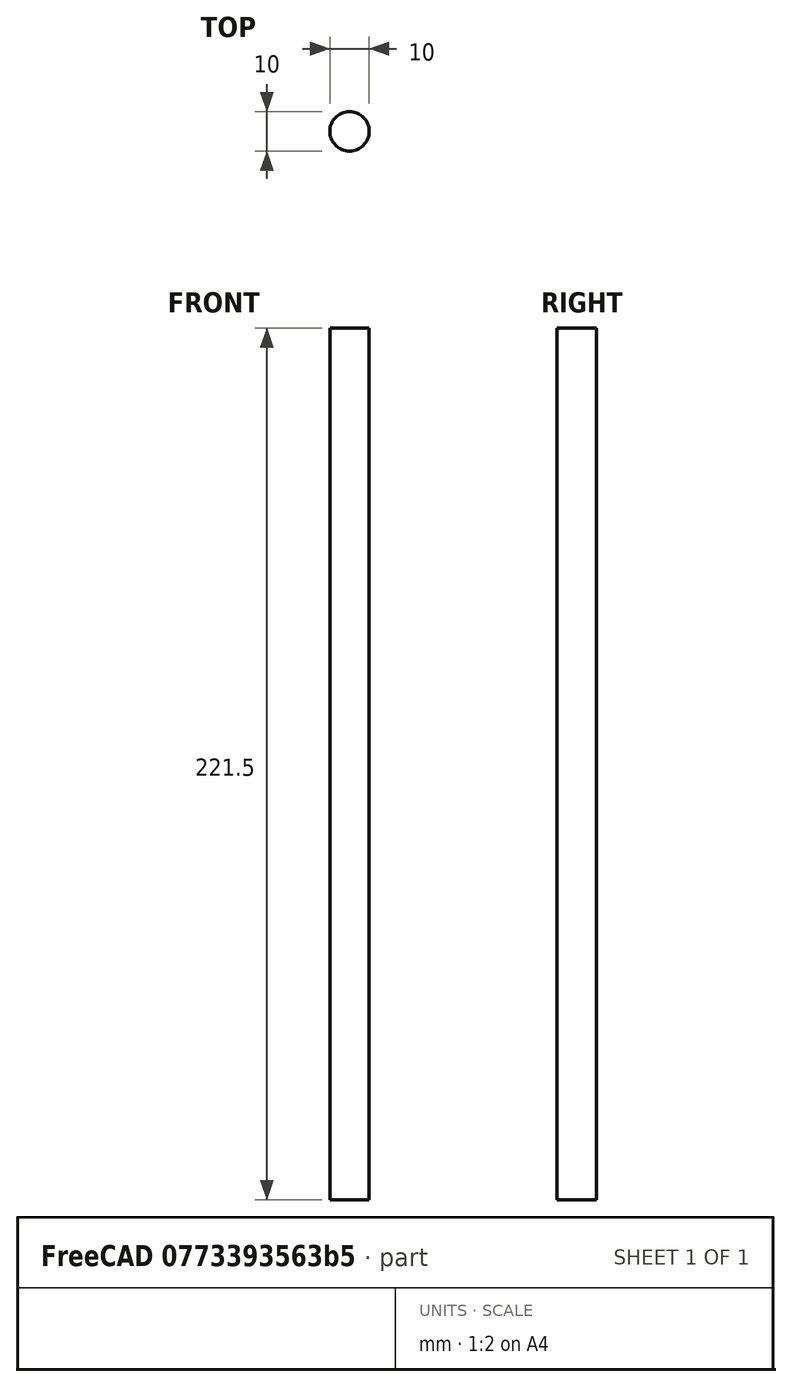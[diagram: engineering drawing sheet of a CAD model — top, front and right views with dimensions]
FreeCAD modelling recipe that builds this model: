
FCSTD DOCUMENT  (FreeCAD 1.0R39109 (Git))
Label: Stator_CoilWinder_Assembly
License: All rights reserved
LicenseURL: http://en.wikipedia.org/wiki/All_rights_reserved
objects: App::Link×12, Part::FeaturePython×8, App::Part×2, Spreadsheet::Sheet×1, Part::Cylinder×1
note: 1 computed .brp shape members not serialized (recipe doc carries the construction recipe); baked Part::Feature solids carry a one-line shape summary decoded from their .brp
EXTERNAL_REF file=Stator_CoilWinder_Cheek.FCStd obj=PolarPattern001Body
EXTERNAL_REF file=Stator_CoilWinder_Spacer.FCStd obj=PadBody001
EXTERNAL_REF file=Stator_CoilWinder_Cheek_Notch.FCStd obj=PolarPattern001Body
EXTERNAL_REF file=../../../Master_of_Puppets.FCStd obj=Alternator
EXTERNAL_REF file=../../../Master_of_Puppets.FCStd obj=Fastener
EXTERNAL_REF file=../../../Master_of_Puppets.FCStd obj=Spreadsheet
EXTERNAL_REF file=../Stator_Coil.FCStd obj=Body001
EXTERNAL_REF file=Stator_CoilWinder_Cheek_Triangular.FCStd obj=PolarPattern001Body
EXTERNAL_REF file=Stator_CoilWinder_Pins_Quadrilateral.FCStd obj=Part
EXTERNAL_REF file=Stator_CoilWinder_Pins_Triangular.FCStd obj=Extrude
EXTERNAL_REF file=Stator_CoilWinder_Spacer_Triangular.FCStd obj=PadBody001
EXTERNAL_REF file=../Stator_Coil_Triangular.FCStd obj=Body
EXTERNAL_REF file=../Stator_Coil_Triangular_Reduced.FCStd obj=Body
EXTERNAL_REF file=../../../Fasteners/Fastener_HexNut_CoilWinder.FCStd obj=Binder
EXTERNAL_REF file=../../../Fasteners/Fastener_Washer_CoilWinder.FCStd obj=Tube

FEATURE [App::Link] Link  label="Stator_CoilWinder_Cheek"
  LinkedObject = -> <external Stator_CoilWinder_Cheek.FCStd>#PolarPattern001Body
  expr: .Placement.Base.z = Spreadsheet.CheekZ
  expr: LinkedObject = Spreadsheet.Stator_CoilWinder_Cheek
FEATURE [App::Link] Link001  label="Stator_CoilWinder_Spacer"
  LinkPlacement = pos=(0,0,12) rot=(0,0,1;0rad)
  LinkedObject = -> <external Stator_CoilWinder_Spacer.FCStd>#PadBody001
  Placement = pos=(0,0,12) rot=(0,0,1;0rad)
  expr: .Placement.Base.z = Spreadsheet.CenterZ
  expr: LinkedObject = Spreadsheet.Stator_CoilWinder_Spacer
FEATURE [App::Link] Link002  label="Stator_CoilWinder_Cheek_Notch"
  LinkPlacement = pos=(0,0,25) rot=(0,0,1;0rad)
  LinkedObject = -> <external Stator_CoilWinder_Cheek_Notch.FCStd>#PolarPattern001Body
  Placement = pos=(0,0,25) rot=(0,0,1;0rad)
  expr: .Placement.Base.z = Spreadsheet.NotchZ
FEATURE [Spreadsheet::Sheet] Spreadsheet
  cells = A1='Inputs; A2='StatorThickness; B2(StatorThickness)==Master_of_Puppets#Spreadsheet.StatorThickness; A3='CoilType; B3(CoilType)==Master_of_Puppets#Spreadsheet.CoilType; A4='CoilWinderCheekThickness; B4(CoilWinderCheekThickness)==Master_of_Puppets#Alternator.CoilWinderCheekThickness; A5='CoilLegWidth; B5(CoilLegWidth)==Master_of_Puppets#Spreadsheet.CoilLegWidth; A6='MagnetWidth; B6(MagnetWidth)==Master_of_Puppets#Spreadsheet.MagnetWidth; A7='MagnetLength; B7(MagnetLength)==Master_of_Puppets#Spreadsheet.MagnetLength; A8='NumberOfCoilsPerPhase; B8(NumberOfCoilsPerPhase)==Master_of_Puppets#Spreadsheet.NumberOfCoilsPerPhase; A9='CoilWinderCenterRodRadius; B9(CoilWinderCenterRodRadius)==Master_of_Puppets#Alternator.CoilWinderCenterRodRadius; A10='CoilWinderHexNutThickness; B10(CoilWinderHexNutThickness)==Master_of_Puppets#Alternator.CoilWinderHexNutThickness; A11='DistanceThreadsExtendFromNuts; B11(DistanceThreadsExtendFromNuts)==Master_of_Puppets#Fastener.DistanceThreadsExtendFromNuts; A12='CoilWinderNumberOfSpacingNuts; B12(CoilWinderNumberOfSpacingNuts)==Master_of_Puppets#Alternator.CoilWinderNumberOfSpacingNuts; A13='CoilWinderSpaceBetweenLayer; B13(CoilWinderSpaceBetweenLayer)==Master_of_Puppets#Alternator.CoilWinderSpaceBetweenLayer; A14='CoilWinderCenterRodLength; B14(CoilWinderCenterRodLength)==Master_of_Puppets#Alternator.CoilWinderCenterRodLength; A15='CoilWinderAssemblyThicknessTotal; B15(CoilWinderAssemblyThicknessTotal)==Master_of_Puppets#Alternator.CoilWinderAssemblyThicknessTotal; A16='CoilWinderNumberOfNutStacks; B16(CoilWinderNumberOfNutStacks)==Master_of_Puppets#Alternator.CoilWinderNumberOfNutStacks; A17='CoilWinderAssemblyThickness; B17(CoilWinderAssemblyThickness)==Master_of_Puppets#Alternator.CoilWinderAssemblyThickness; A18='CoilWinderCoilsAngle; B18(CoilWinderCoilsAngle)==Master_of_Puppets#Alternator.CoilWinderCoilsAngle; A19='DoCoilsOverlap; B19(DoCoilsOverlap)==Master_of_Puppets#Alternator.DoCoilsOverlap; A20='TriangularCoilWinderCircumradius; B20(TriangularCoilWinderCircumradius)==Master_of_Puppets#Alternator.TriangularCoilWinderCircumradius; A21='WasherThickness; B21(WasherThickness)==Master_of_Puppets#Fastener.WasherThickness; A22='Calculated; A23='SpaceBetweenLayers; B23(SpaceBetweenLayers)=0; A24='CheekZ; B24(CheekZ)=0; A25='CenterZ; B25(CenterZ)==CoilWinderCheekThickness + SpaceBetweenLayers; A26='NotchZ; B26(NotchZ)==CenterZ + StatorThickness + SpaceBetweenLayers; A27='Stator_CoilWinder_Cheek; B27(Stator_CoilWinder_Cheek)==CoilType != 3 ? <<Stator_CoilWinder_Cheek>>#<<Stator_CoilWinder_Cheek>>._self : <<Stator_CoilWinder_Cheek_Triangular>>#<<Stator_CoilWinder_Cheek>>._self; A28='Stator_CoilWinder_Spacer; B28(Stator_CoilWinder_Spacer)==CoilType != 3 ? <<Stator_CoilWinder_Spacer>>#<<Stator_CoilWinder_Spacer>>._self : <<Stator_CoilWinder_Spacer_Triangular>>#<<Stator_CoilWinder_Spacer>>._self; A29='Stator_Coil; B29(Stator_Coil)==CoilType != 3 ? <<Stator_Coil>>#<<Stator_Coil>>._self : (DoCoilsOverlap == 1 ? <<Stator_Coil_Triangular_Reduced>>#<<Stator_Coil>>._self : <<Stator_Coil_Triangular>>#<<Stator_Coil>>._self); A30='CoilY; B30(CoilY)==CoilType != 3 ? -(MagnetLength / 2) - CoilLegWidth : -TriangularCoilWinderCircumradius; A31='RodZ; B31(RodZ)==-WasherThickness - CoilWinderHexNutThickness - DistanceThreadsExtendFromNuts; A32='BackWasherNutStackZ; B32(BackWasherNutStackZ)==CoilWinderAssemblyThickness + SpaceBetweenLayers; A33='NutStackZ; B33(NutStackZ)==BackWasherNutStackZ + WasherThickness; A34='FrontWasherNutStackZ; B34(FrontWasherNutStackZ)==NutStackZ + CoilWinderNumberOfSpacingNuts * CoilWinderHexNutThickness; A35='OuterFrontWasherZ; B35(OuterFrontWasherZ)==CoilWinderAssemblyThicknessTotal + SpaceBetweenLayers; A36='NutOuter2Z; B36(NutOuter2Z)==OuterFrontWasherZ + WasherThickness; A37='Pins; B37(Pins)==CoilType != 3 ? <<Stator_CoilWinder_Pins_Quadrilateral>>#<<Stator_CoilWinder_Pins>>._self : <<Stator_CoilWinder_Pins_Triangular>>#<<Stator_CoilWinder_Pins>>._self; A38='PinsZ; B38(PinsZ)==-DistanceThreadsExtendFromNuts; A39='OuterBackNutZ; B39(OuterBackNutZ)==-CoilWinderHexNutThickness - WasherThickness
FEATURE [App::Link] Link003  label="Stator_Coil"
  LinkPlacement = pos=(0,-33.52,12) rot=(0,0,1;0rad)
  LinkedObject = -> <external ../Stator_Coil.FCStd>#Body001
  Placement = pos=(0,-33.52,12) rot=(0,0,1;0rad)
  expr: .Placement.Base.y = Spreadsheet.CoilY
  expr: .Placement.Base.z = Spreadsheet.CenterZ
  expr: LinkedObject = Spreadsheet.Stator_Coil
FEATURE [Part::Cylinder] Cylinder  label="CenterRod"
  Angle = 360
  AttacherType = Attacher::AttachEngine3D
  FirstAngle = 0
  Height = 221.5
  Placement = pos=(0,0,-16.05) rot=(0,0,1;0rad)
  Radius = 5
  SecondAngle = 0
  expr: .Placement.Base.z = Spreadsheet.RodZ
  expr: Height = Spreadsheet.CoilWinderCenterRodLength
  expr: Radius = Spreadsheet.CoilWinderCenterRodRadius
FEATURE [App::Link] Link004  label="Outer_Nut_Back"
  LinkPlacement = pos=(0,0,-11.05) rot=(0,0,1;0rad)
  LinkedObject = -> <external ../../../Fasteners/Fastener_HexNut_CoilWinder.FCStd>#Binder
  Placement = pos=(0,0,-11.05) rot=(0,0,1;0rad)
  expr: .Placement.Base.z = Spreadsheet.OuterBackNutZ
FEATURE [App::Link] Link005  label="Fastener_HexNut_Spacing"
  LinkedObject = -> Link004
FEATURE [Part::FeaturePython] Array  label="NutStack"  # Draft array (typed FeaturePython)
  AlwaysSyncPlacement = false
  Angle = 360
  ArrayType = 0
  Axis = (0,0,1)
  Base = -> Link005
  Center = (0,0,0)
  Count = 4
  ExpandArray = false
  Fuse = false
  IntervalAxis = (0,0,0)
  IntervalX = (100,0,0)
  IntervalY = (0,100,0)
  IntervalZ = (0,0,8.55)
  NumberCircles = 3
  NumberPolar = 5
  NumberX = 1
  NumberY = 1
  NumberZ = 4
  Placement = pos=(0,0,39.5) rot=(0,0,1;0rad)
  PlacementList = 4 placements: arithmetic series from (0,0,0) step (0,0,8.55) to (0,0,25.65)
  RadialDistance = 50
  ScaleList = (4) [(1,1,1),(1,1,1),(1,1,1),(1,1,1)]
  Symmetry = 1
  TangentialDistance = 25
  expr: .IntervalZ.z = Spreadsheet.CoilWinderHexNutThickness
  expr: .Placement.Base.z = Spreadsheet.NutStackZ
  expr: NumberZ = Spreadsheet.CoilWinderNumberOfSpacingNuts
FEATURE [App::Link] Link006  label="Outer_Nut_Front"
  LinkPlacement = pos=(0,0,191.9) rot=(0,0,1;0rad)
  LinkedObject = -> Link004
  Placement = pos=(0,0,191.9) rot=(0,0,1;0rad)
  expr: .Placement.Base.z = Spreadsheet.NutOuter2Z
FEATURE [Part::FeaturePython] Array003  label="Stator_CoilWinder_Cheeks"  # Draft array (typed FeaturePython)
  AlwaysSyncPlacement = false
  Angle = 360
  ArrayType = 0
  Axis = (0,0,1)
  Base = -> Link
  Center = (0,0,0)
  Count = 3
  ExpandArray = false
  Fuse = false
  IntervalAxis = (0,0,0)
  IntervalX = (100,0,0)
  IntervalY = (0,100,0)
  IntervalZ = (0,0,76.2)
  NumberCircles = 3
  NumberPolar = 5
  NumberX = 1
  NumberY = 1
  NumberZ = 3
  PlacementList = 3 placements: arithmetic series from (0,0,0) step (0,0,76.2) to (0,0,152.4)
  RadialDistance = 50
  ScaleList = (3) [(1,1,1),(1,1,1),(1,1,1)]
  Symmetry = 1
  TangentialDistance = 25
  expr: .IntervalZ.z = Spreadsheet.CoilWinderSpaceBetweenLayer
  expr: NumberZ = Spreadsheet.NumberOfCoilsPerPhase
FEATURE [Part::FeaturePython] Array004  label="Stator_CoilWinder_Cheek_Spacers"  # Draft array (typed FeaturePython)
  AlwaysSyncPlacement = false
  Angle = 360
  ArrayType = 0
  Axis = (0,0,1)
  Base = -> Link001
  Center = (0,0,0)
  Count = 3
  ExpandArray = false
  Fuse = false
  IntervalAxis = (0,0,0)
  IntervalX = (100,0,0)
  IntervalY = (0,100,0)
  IntervalZ = (0,0,76.2)
  NumberCircles = 3
  NumberPolar = 5
  NumberX = 1
  NumberY = 1
  NumberZ = 3
  PlacementList = 3 placements: arithmetic series from (0,0,12) step (0,0,76.2) to (0,0,164.4)
  RadialDistance = 50
  ScaleList = (3) [(1,1,1),(1,1,1),(1,1,1)]
  Symmetry = 1
  TangentialDistance = 25
  expr: .IntervalZ.z = Spreadsheet.CoilWinderSpaceBetweenLayer
  expr: NumberZ = Spreadsheet.NumberOfCoilsPerPhase
FEATURE [Part::FeaturePython] Array005  label="Stator_CoilWinder_Cheek_Notches"  # Draft array (typed FeaturePython)
  AlwaysSyncPlacement = false
  Angle = 360
  ArrayType = 0
  Axis = (0,0,1)
  Base = -> Link002
  Center = (0,0,0)
  Count = 3
  ExpandArray = false
  Fuse = false
  IntervalAxis = (0,0,0)
  IntervalX = (100,0,0)
  IntervalY = (0,100,0)
  IntervalZ = (0,0,76.2)
  NumberCircles = 3
  NumberPolar = 5
  NumberX = 1
  NumberY = 1
  NumberZ = 3
  PlacementList = 3 placements: arithmetic series from (0,0,25) step (0,0,76.2) to (0,0,177.4)
  RadialDistance = 50
  ScaleList = (3) [(1,1,1),(1,1,1),(1,1,1)]
  Symmetry = 1
  TangentialDistance = 25
  expr: .IntervalZ.z = Spreadsheet.CoilWinderSpaceBetweenLayer
  expr: NumberZ = Spreadsheet.NumberOfCoilsPerPhase
FEATURE [Part::FeaturePython] Array006  label="Stator_Coils"  # Draft array (typed FeaturePython)
  AlwaysSyncPlacement = false
  Angle = 360
  ArrayType = 0
  Axis = (0,0,1)
  Base = -> Link003
  Center = (0,0,0)
  Count = 3
  ExpandArray = false
  Fuse = false
  IntervalAxis = (0,0,0)
  IntervalX = (100,0,0)
  IntervalY = (0,100,0)
  IntervalZ = (0,0,76.2)
  NumberCircles = 3
  NumberPolar = 5
  NumberX = 1
  NumberY = 1
  NumberZ = 3
  Placement = pos=(0,0,0) rot=(0,0,1;1.5708rad)
  PlacementList = 3 placements: arithmetic series from (0,-33.52,12) step (0,0,76.2) to (0,-33.52,164.4)
  RadialDistance = 50
  ScaleList = (3) [(1,1,1),(1,1,1),(1,1,1)]
  Symmetry = 1
  TangentialDistance = 25
  expr: .IntervalZ.z = Spreadsheet.CoilWinderSpaceBetweenLayer
  expr: .Placement.Rotation.Angle = Spreadsheet.CoilWinderCoilsAngle
  expr: NumberZ = Spreadsheet.NumberOfCoilsPerPhase
FEATURE [App::Link] Link007  label="Pins"
  LinkPlacement = pos=(0,0,-5) rot=(0,0,1;0rad)
  LinkedObject = -> <external Stator_CoilWinder_Pins_Quadrilateral.FCStd>#Part
  Placement = pos=(0,0,-5) rot=(0,0,1;0rad)
  expr: .Placement.Base.z = Spreadsheet.PinsZ
  expr: LinkedObject = Spreadsheet.Pins
FEATURE [App::Part] Part003  label="Rods"
  Group = -> [Cylinder,Link007]
  Origin = -> Origin003
FEATURE [App::Link] Link008  label="Outer_Washer_Back"
  LinkPlacement = pos=(0,0,-2.5) rot=(0,0,1;0rad)
  LinkedObject = -> <external ../../../Fasteners/Fastener_Washer_CoilWinder.FCStd>#Tube
  Placement = pos=(0,0,-2.5) rot=(0,0,1;0rad)
  expr: .Placement.Base.z = -Spreadsheet.WasherThickness
FEATURE [App::Link] Link009  label="Outer_Washer_Front"
  LinkPlacement = pos=(0,0,189.4) rot=(0,0,1;0rad)
  LinkedObject = -> Link008
  Placement = pos=(0,0,189.4) rot=(0,0,1;0rad)
  expr: .Placement.Base.z = Spreadsheet.OuterFrontWasherZ
FEATURE [App::Link] Link010  label="Washer_Back_Inner"
  LinkPlacement = pos=(0,0,37) rot=(0,0,1;0rad)
  LinkedObject = -> Link008
  Placement = pos=(0,0,37) rot=(0,0,1;0rad)
  expr: .Placement.Base.z = Spreadsheet.BackWasherNutStackZ
FEATURE [App::Link] Link011  label="Washer_Front_Inner"
  LinkPlacement = pos=(0,0,73.7) rot=(0,0,1;0rad)
  LinkedObject = -> Link010
  Placement = pos=(0,0,73.7) rot=(0,0,1;0rad)
  expr: .Placement.Base.z = Spreadsheet.FrontWasherNutStackZ
FEATURE [Part::FeaturePython] Array007  label="NutStacks"  # Draft array (typed FeaturePython)
  AlwaysSyncPlacement = false
  Angle = 360
  ArrayType = 0
  Axis = (0,0,1)
  Base = -> Array
  Center = (0,0,0)
  Count = 2
  ExpandArray = false
  Fuse = false
  IntervalAxis = (0,0,0)
  IntervalX = (0,0,0)
  IntervalY = (0,100,0)
  IntervalZ = (0,0,76.2)
  NumberCircles = 3
  NumberPolar = 5
  NumberX = 1
  NumberY = 1
  NumberZ = 2
  PlacementList = 2 placements: [(0,0,39.5),(0,0,115.7)]
  RadialDistance = 50
  ScaleList = (2) [(1,1,1),(1,1,1)]
  Symmetry = 1
  TangentialDistance = 25
  expr: .IntervalZ.z = Spreadsheet.CoilWinderSpaceBetweenLayer
  expr: NumberZ = Spreadsheet.CoilWinderNumberOfNutStacks
FEATURE [Part::FeaturePython] Array008  label="InnerBackWashers"  # Draft array (typed FeaturePython)
  AlwaysSyncPlacement = false
  Angle = 360
  ArrayType = 0
  Axis = (0,0,1)
  Base = -> Link010
  Center = (0,0,0)
  Count = 2
  ExpandArray = false
  Fuse = false
  IntervalAxis = (0,0,0)
  IntervalX = (100,0,0)
  IntervalY = (0,100,0)
  IntervalZ = (0,0,76.2)
  NumberCircles = 3
  NumberPolar = 5
  NumberX = 1
  NumberY = 1
  NumberZ = 2
  PlacementList = 2 placements: [(0,0,37),(0,0,113.2)]
  RadialDistance = 50
  ScaleList = (2) [(1,1,1),(1,1,1)]
  Symmetry = 1
  TangentialDistance = 25
  expr: .IntervalZ.z = Spreadsheet.CoilWinderSpaceBetweenLayer
  expr: NumberZ = Spreadsheet.CoilWinderNumberOfNutStacks
FEATURE [Part::FeaturePython] Array009  label="InnerFrontWashers"  # Draft array (typed FeaturePython)
  AlwaysSyncPlacement = false
  Angle = 360
  ArrayType = 0
  Axis = (0,0,1)
  Base = -> Link011
  Center = (0,0,0)
  Count = 2
  ExpandArray = false
  Fuse = false
  IntervalAxis = (0,0,0)
  IntervalX = (100,0,0)
  IntervalY = (0,100,0)
  IntervalZ = (0,0,76.2)
  NumberCircles = 3
  NumberPolar = 5
  NumberX = 1
  NumberY = 1
  NumberZ = 2
  PlacementList = 2 placements: [(0,0,73.7),(0,0,149.9)]
  RadialDistance = 50
  ScaleList = (2) [(1,1,1),(1,1,1)]
  Symmetry = 1
  TangentialDistance = 25
  expr: .IntervalZ.z = Spreadsheet.CoilWinderSpaceBetweenLayer
  expr: NumberZ = Spreadsheet.CoilWinderNumberOfNutStacks
FEATURE [App::Part] Part  label="Stator_CoilWinder_Assembly"
  Group = -> [Link,Array003,Link001,Array004,Link003,Array006,Link002,Array005,Link004,Part003,Link008,Link009,Link006,Link010,Array008,Link005,Array,Array007,Link011,Array009]
  Origin = -> Origin

RESOLVED EXTERNAL PARTS (link-assembly join: the EXTERNAL_REF files above that resolve inside this repo's crawl, each included once):
---- part ../../../Fasteners/Fastener_HexNut_CoilWinder.FCStd = doc fcstd_accbea4014fd ----
FCSTD DOCUMENT  (FreeCAD 0.20R29177 (Git))
Label: Fastener_HexNut_CoilWinder
License: All rights reserved
LicenseURL: http://en.wikipedia.org/wiki/All_rights_reserved
objects: PartDesign::SubShapeBinder×1
note: 1 computed .brp shape members not serialized (recipe doc carries the construction recipe); baked Part::Feature solids carry a one-line shape summary decoded from their .brp
EXTERNAL_REF file=Fastener_HexNut.FCStd obj=Body

FEATURE [PartDesign::SubShapeBinder] Binder  label="Fastener_HexNut"
  BindCopyOnChange = 2
  BindMode = 0
  ClaimChildren = false
  Fuse = false
  MakeFace = true
  OffsetFill = false
  OffsetIntersection = false
  OffsetJoinType = 0
  OffsetOpenResult = false
  PartialLoad = false
  Relative = true
  Support = -> [<external Fastener_HexNut.FCStd>#Body]
  Variant = 3
  _Version = 2
---- part ../../../Master_of_Puppets.FCStd = doc fcstd_6404554055c4 (61625 chars; too large to inline — full recipe in that document) ----
---- part ../Stator_Coil.FCStd = doc fcstd_4f31de19f594 ----
FCSTD DOCUMENT  (FreeCAD 0.21R33771 (Git))
Label: Stator_Coil
License: All rights reserved
LicenseURL: http://en.wikipedia.org/wiki/All_rights_reserved
objects: Sketcher::SketchObject×1, PartDesign::Pad×1, Spreadsheet::Sheet×1, PartDesign::Mirrored×1, PartDesign::Body×1, Part::Refine×1
note: 6 computed .brp shape members not serialized (recipe doc carries the construction recipe); baked Part::Feature solids carry a one-line shape summary decoded from their .brp
EXTERNAL_REF file=../../Master_of_Puppets.FCStd obj=Alternator
EXTERNAL_REF file=../../Master_of_Puppets.FCStd obj=Spreadsheet

FEATURE [Sketcher::SketchObject] Sketch
  FullyConstrained = true
  MapMode = 5
  Support = -> [XY_Plane]
  expr: Constraints[13] = Spreadsheet.CoilLegWidth
  expr: Constraints[27] = Spreadsheet.CoilHoleWidthAtOuterRadius / 2 - Spreadsheet.CoilWinderPinRadius
  expr: Constraints[30] = Spreadsheet.CoilHoleWidthAtInnerRadius / 2 - Spreadsheet.CoilWinderPinRadius
  expr: Constraints[31] = Spreadsheet.CoilLegWidth
  expr: Constraints[32] = Spreadsheet.CoilLegWidth
  expr: Constraints[4] = Spreadsheet.CoilWinderPinRadius
  expr: Constraints[5] = Spreadsheet.HoleLength
  sketch-geometry (12):
    g0: LineSegment StartX=0 StartY=89.13 StartZ=0 EndX=14.815 EndY=89.13 EndZ=0
    g1: LineSegment StartX=17.2898 StartY=86.2756 StartZ=0 EndX=9.69975 EndY=33.2756 EndZ=0
    g2: LineSegment StartX=7.225 StartY=31.13 StartZ=0 EndX=0 EndY=31.13 EndZ=0
    g3: ArcOfCircle CenterX=14.815 CenterY=86.63 CenterZ=0 NormalX=0 NormalY=0 NormalZ=1 AngleXU=0 Radius=2.5 StartAngle=6.14094 EndAngle=7.85398
    g4: ArcOfCircle CenterX=7.225 CenterY=33.63 CenterZ=0 NormalX=0 NormalY=0 NormalZ=1 AngleXU=0 Radius=2.5 StartAngle=4.71239 EndAngle=6.14094
    g5: LineSegment StartX=0 StartY=120.26 StartZ=0 EndX=17.6214 EndY=120.26 EndZ=0
    g6: LineSegment StartX=48.437 StartY=84.717 StartZ=0 EndX=40.131 EndY=26.717 EndZ=0
    g7: LineSegment StartX=9.31539 StartY=0 StartZ=0 EndX=0 EndY=0 EndZ=0
    g8: ArcOfCircle CenterX=17.6214 CenterY=89.13 CenterZ=0 NormalX=0 NormalY=0 NormalZ=1 AngleXU=0 Radius=31.13 StartAngle=6.14094 EndAngle=7.85398
    g9: ArcOfCircle CenterX=9.31539 CenterY=31.13 CenterZ=0 NormalX=0 NormalY=0 NormalZ=1 AngleXU=0 Radius=31.13 StartAngle=4.71239 EndAngle=6.14094
    g10: LineSegment StartX=0 StartY=120.26 StartZ=0 EndX=0 EndY=89.13 EndZ=0
    g11: LineSegment StartX=0 StartY=31.13 StartZ=0 EndX=0 EndY=0 EndZ=0
  constraints (33):
    c: Horizontal(g0)
    c: Horizontal(g2)
    c: Tangent(g1,g3) = 1.5708
    c: Tangent(g1,g4) = 1.5708
    c: Radius(g3) = 2.5
    c: DistanceY(g2,g0) = 58
    c: Horizontal(g5)
    c: Horizontal(g7)
    c: Parallel(g1,g6)
    c: Tangent(g5,g8) = 1.5708
    c: Tangent(g6,g8) = 1.5708
    c: Tangent(g6,g9) = 1.5708
    c: Tangent(g7,g9) = 1.5708
    c: Radius(g8) = 31.13
    c: Coincident(g7,g-1)
    c: PointOnObject(g2,g-2)
    c: PointOnObject(g0,g-2)
    c: PointOnObject(g5,g-2)
    c: Coincident(g10,g5)
    c: Coincident(g10,g0)
    c: Coincident(g11,g2)
    c: Coincident(g11,g7)
    c: Equal(g4,g3)
    c: Equal(g8,g9)
    c: Equal(g11,g10)
    c: Vertical(g0,g3)
    c: Coincident(g3,g0)
    c: DistanceX(g0,g0) = 14.815
    c: Coincident(g2,g4)
    c: Vertical(g4,g2)
    c: DistanceX(g2,g2) = 7.225
    c: DistanceY(g7,g2) = 31.13
    c: Distance(g6,g1) = 31.13
FEATURE [PartDesign::Pad] Pad
  AllowMultiFace = false
  Direction = (0,0,1)
  Length = 14.8
  Length2 = 100
  Profile = -> Sketch
  Type = 0
  expr: Length = Spreadsheet.CoilThickness
FEATURE [Spreadsheet::Sheet] Spreadsheet
  cells = A1='Inputs; A2='CoilLegWidth; B2(CoilLegWidth)==Master_of_Puppets#Spreadsheet.CoilLegWidth; A3='MagnetLength; B3(MagnetLength)==Master_of_Puppets#Spreadsheet.MagnetLength; A4='CoilHoleWidthAtOuterRadius; B4(CoilHoleWidthAtOuterRadius)==Master_of_Puppets#Spreadsheet.CoilHoleWidthAtOuterRadius; A5='CoilHoleWidthAtInnerRadius; B5(CoilHoleWidthAtInnerRadius)==Master_of_Puppets#Spreadsheet.CoilHoleWidthAtInnerRadius; A6='CoilWinderPinRadius; B6(CoilWinderPinRadius)==Master_of_Puppets#Alternator.CoilWinderPinRadius; A7='CoilThickness; B7(CoilThickness)==Master_of_Puppets#Alternator.CoilThickness; A8='Calculated; A9='HoleLength; B9(HoleLength)==MagnetLength; A10='MiddleLength; B10(MiddleLength)==CoilLegWidth + HoleLength / 2
FEATURE [PartDesign::Mirrored] Mirrored
  BaseFeature = -> Pad
  MirrorPlane = -> Sketch [V_Axis]
  Originals = -> [Pad]
FEATURE [PartDesign::Body] Body
  Group = -> [Sketch,Pad,Mirrored]
  Origin = -> Origin
  Tip = -> Mirrored
FEATURE [Part::Refine] Body001  label="Stator_Coil"
  Source = -> Body
---- part ../Stator_Coil_Triangular.FCStd = doc fcstd_6ed8b2cba0b0 ----
FCSTD DOCUMENT  (FreeCAD 0.21R33771 (Git))
Label: Stator_Coil_Triangular
License: All rights reserved
LicenseURL: http://en.wikipedia.org/wiki/All_rights_reserved
objects: Sketcher::SketchObject×1, PartDesign::Pad×1, PartDesign::Body×1, Spreadsheet::Sheet×1
note: 4 computed .brp shape members not serialized (recipe doc carries the construction recipe); baked Part::Feature solids carry a one-line shape summary decoded from their .brp
EXTERNAL_REF file=../../Master_of_Puppets.FCStd obj=Alternator
EXTERNAL_REF file=../../Master_of_Puppets.FCStd obj=Spreadsheet

FEATURE [Sketcher::SketchObject] Sketch
  FullyConstrained = true
  MapMode = 5
  Support = -> [XY_Plane]
  expr: Constraints[0] = Spreadsheet.CoilWinderPinRadius
  expr: Constraints[15] = Spreadsheet.CoilLegWidth
  expr: Constraints[25] = Spreadsheet.MagnetWidth
  expr: Constraints[29] = Spreadsheet.MagnetLength
  expr: Constraints[2] = Spreadsheet.InnerBottomArcRadius
  sketch-geometry (18):
    g0: Circle CenterX=-22.5 CenterY=72.5 CenterZ=0 NormalX=0 NormalY=0 NormalZ=1 AngleXU=0 Radius=2.5
    g1: Circle CenterX=22.5 CenterY=72.5 CenterZ=0 NormalX=0 NormalY=0 NormalZ=1 AngleXU=0 Radius=2.5
    g2: Circle CenterX=0 CenterY=4 CenterZ=0 NormalX=0 NormalY=0 NormalZ=1 AngleXU=0 Radius=4
    g3: LineSegment StartX=3.82539 StartY=2.83108 StartZ=0 EndX=24.8909 EndY=71.7694 EndZ=0
    g4: LineSegment StartX=-22.5 StartY=75 StartZ=0 EndX=22.5 EndY=75 EndZ=0
    g5: LineSegment StartX=-3.82539 StartY=2.83108 StartZ=0 EndX=-24.8909 EndY=71.7694 EndZ=0
    g6: ArcOfCircle CenterX=0 CenterY=4 CenterZ=0 NormalX=0 NormalY=0 NormalZ=1 AngleXU=0 Radius=4 StartAngle=3.43815 EndAngle=5.98663
    g7: LineSegment StartX=-22.5 StartY=100.92 StartZ=0 EndX=22.5 EndY=100.92 EndZ=0
    g8: LineSegment StartX=-49.6794 StartY=64.1948 StartZ=0 EndX=-28.6139 EndY=-4.74355 EndZ=0
    g9: LineSegment StartX=49.6794 StartY=64.1948 StartZ=0 EndX=28.6139 EndY=-4.74355 EndZ=0
    g10: ArcOfCircle CenterX=-22.5 CenterY=72.5 CenterZ=0 NormalX=0 NormalY=0 NormalZ=1 AngleXU=0 Radius=28.42 StartAngle=1.5708 EndAngle=3.43815
    g11: ArcOfCircle CenterX=22.5 CenterY=72.5 CenterZ=0 NormalX=0 NormalY=0 NormalZ=1 AngleXU=0 Radius=28.42 StartAngle=5.98663 EndAngle=7.85398
    g12: ArcOfCircle CenterX=0 CenterY=4 CenterZ=0 NormalX=0 NormalY=0 NormalZ=1 AngleXU=0 Radius=29.92 StartAngle=3.43815 EndAngle=5.98663
    g13: ArcOfCircle CenterX=-22.5 CenterY=72.5 CenterZ=0 NormalX=0 NormalY=0 NormalZ=1 AngleXU=0 Radius=2.5 StartAngle=1.5708 EndAngle=3.14159
    g14: ArcOfCircle CenterX=-22.5 CenterY=72.5 CenterZ=0 NormalX=0 NormalY=0 NormalZ=1 AngleXU=0 Radius=2.5 StartAngle=3.14159 EndAngle=3.43815
    g15: ArcOfCircle CenterX=22.5 CenterY=72.5 CenterZ=0 NormalX=0 NormalY=0 NormalZ=1 AngleXU=0 Radius=2.5 StartAngle=5.98663 EndAngle=6.28319
    g16: ArcOfCircle CenterX=22.5 CenterY=72.5 CenterZ=0 NormalX=0 NormalY=0 NormalZ=1 AngleXU=0 Radius=2.5 StartAngle=9e-16 EndAngle=1.5708
    g17: GeomPoint X=-22.5 Y=75 Z=0
  constraints (39):
    c: Radius(g0) = 2.5
    c: Equal(g1,g0)
    c: Radius(g2) = 4
    c: Tangent(g3,g1) = -1.5708
    c: Tangent(g5,g0) = 1.5708
    c: Coincident(g6,g2)
    c: Horizontal(g4)
    c: Equal(g6,g2)
    c: Tangent(g6,g5) = 1.5708
    c: Tangent(g3,g6) = -1.5708
    c: Tangent(g4,g0) = 1.5708
    c: Horizontal(g7)
    c: Parallel(g9,g3)
    c: Tangent(g12,g9) = 1.5708
    c: Tangent(g12,g8) = -1.5708
    c: DistanceY(g4,g7) = 25.92
    c: Tangent(g10,g7) = 1.5708
    c: Tangent(g10,g8) = -1.5708
    c: Tangent(g11,g9) = 1.5708
    c: Tangent(g11,g7) = 1.5708
    c: Coincident(g13,g10)
    c: Coincident(g13,g4)
    c: Coincident(g14,g5)
    c: Coincident(g15,g11)
    c: Coincident(g15,g3)
    c: DistanceX(g13,g15) = 50
    c: Horizontal(g15,g13)
    c: Tangent(g14,g13) = -1.5708
    c: Coincident(g14,g0)
    c: Distance(g-1,g4) = 75
    c: Coincident(g6,g12)
    c: PointOnObject(g6,g-2)
    c: Tangent(g16,g15) = -1.5708
    c: Coincident(g1,g11)
    c: Tangent(g16,g4) = 1.5708
    c: Horizontal(g15,g11)
    c: Coincident(g17,g4)
    c: Symmetric(g10,g11,g-2)
    c: PointOnObject(g-1,g6)
FEATURE [PartDesign::Pad] Pad
  AllowMultiFace = false
  Direction = (0,0,1)
  Length = 13.8
  Length2 = 100
  Profile = -> Sketch
  Type = 0
  expr: Length = Spreadsheet.CoilThickness
FEATURE [PartDesign::Body] Body  label="Stator_Coil"
  Group = -> [Sketch,Pad]
  Origin = -> Origin
  Tip = -> Pad
FEATURE [Spreadsheet::Sheet] Spreadsheet
  cells = A1='Inputs; A2='CoilLegWidth; B2(CoilLegWidth)==Master_of_Puppets#Spreadsheet.CoilLegWidth; A3='CoilHoleWidthAtOuterRadius; B3(CoilHoleWidthAtOuterRadius)==Master_of_Puppets#Spreadsheet.CoilHoleWidthAtOuterRadius; A4='CoilHoleWidthAtInnerRadius; B4(CoilHoleWidthAtInnerRadius)==Master_of_Puppets#Spreadsheet.CoilHoleWidthAtInnerRadius; A5='MagnetWidth; B5(MagnetWidth)==Master_of_Puppets#Spreadsheet.MagnetWidth; A6='CoilWinderPinRadius; B6(CoilWinderPinRadius)==Master_of_Puppets#Alternator.CoilWinderPinRadius; A7='CoilThickness; B7(CoilThickness)==Master_of_Puppets#Alternator.CoilThickness; A8='MagnetLength; B8(MagnetLength)==Master_of_Puppets#Alternator.MagnetLength; A9='CoilType; B9(CoilType)==Master_of_Puppets#Alternator.CoilType; A10='Calculated; A11='InnerBottomArcRadius; B11(InnerBottomArcRadius)==CoilType == 3 ? CoilHoleWidthAtInnerRadius / 2 : 4; C11='Duplicated in Stator_Coil_Triangular_Reduced
---- part ../Stator_Coil_Triangular_Reduced.FCStd = doc fcstd_347f9b8b952c ----
FCSTD DOCUMENT  (FreeCAD 1.0R39109 (Git))
Label: Stator_Coil_Triangular_Reduced
License: All rights reserved
LicenseURL: http://en.wikipedia.org/wiki/All_rights_reserved
objects: Sketcher::SketchObject×1, PartDesign::Pad×1, PartDesign::Body×1, Spreadsheet::Sheet×1
note: 6 computed .brp shape members not serialized (recipe doc carries the construction recipe); baked Part::Feature solids carry a one-line shape summary decoded from their .brp
EXTERNAL_REF file=../../Master_of_Puppets.FCStd obj=Alternator
EXTERNAL_REF file=../../Master_of_Puppets.FCStd obj=Spreadsheet

FEATURE [Sketcher::SketchObject] Sketch
  ArcFitTolerance = 0
  AttachmentSupport = -> [XY_Plane]
  FullyConstrained = true
  MakeInternals = false
  MapMode = 5
  expr: Constraints[25] = Spreadsheet.CoilLegWidth
  expr: Constraints[27] = Spreadsheet.CoilLegWidth
  expr: Constraints[2] = Spreadsheet.CoilWinderPinRadius
  expr: Constraints[33] = Spreadsheet.CornerCircleRadius
  expr: Constraints[34] = Spreadsheet.CornerCircleRadius
  expr: Constraints[35] = Spreadsheet.CornerCircleRadius
  expr: Constraints[60] = Spreadsheet.CoilLegWidth
  expr: Constraints[61] = Spreadsheet.VerticalDimension
  expr: Constraints[63] = Spreadsheet.HorizontalDistanceBetweenPins
  expr: Constraints[6] = Spreadsheet.InnerBottomArcRadius
  sketch-geometry (24):
    g0: Circle [constr] CenterX=0 CenterY=18.125 CenterZ=0 NormalX=0 NormalY=0 NormalZ=1 AngleXU=0 Radius=18.125
    g1: Circle [constr] CenterX=-12.5 CenterY=27.5 CenterZ=0 NormalX=0 NormalY=0 NormalZ=1 AngleXU=0 Radius=2.5
    g2: Circle [constr] CenterX=12.5 CenterY=27.5 CenterZ=0 NormalX=0 NormalY=0 NormalZ=1 AngleXU=0 Radius=2.5
    g3: Circle [constr] CenterX=0 CenterY=4 CenterZ=0 NormalX=0 NormalY=0 NormalZ=1 AngleXU=0 Radius=4
    g4: LineSegment StartX=3.63174 StartY=2.32355 StartZ=0 EndX=14.7698 EndY=26.4522 EndZ=0
    g5: LineSegment StartX=-12.5 StartY=30 StartZ=0 EndX=12.5 EndY=30 EndZ=0
    g6: LineSegment StartX=-3.63174 StartY=2.32355 StartZ=0 EndX=-14.7698 EndY=26.4522 EndZ=0
    g7: ArcOfCircle CenterX=-12.5 CenterY=27.5 CenterZ=0 NormalX=0 NormalY=0 NormalZ=1 AngleXU=0 Radius=2.5 StartAngle=1.5708 EndAngle=3.57406
    g8: ArcOfCircle CenterX=12.5 CenterY=27.5 CenterZ=0 NormalX=0 NormalY=0 NormalZ=1 AngleXU=0 Radius=2.5 StartAngle=5.85072 EndAngle=7.85398
    g9: ArcOfCircle CenterX=0 CenterY=4 CenterZ=0 NormalX=0 NormalY=0 NormalZ=1 AngleXU=0 Radius=4 StartAngle=3.57406 EndAngle=5.85072
    g10: LineSegment [constr] StartX=10.9259 StartY=18.125 StartZ=0 EndX=20.0052 EndY=13.9339 EndZ=0
    g11: LineSegment [constr] StartX=-10.9259 StartY=18.125 StartZ=0 EndX=-20.0052 EndY=13.9339 EndZ=0
    g12: Circle [constr] CenterX=-14.5 CenterY=29 CenterZ=0 NormalX=0 NormalY=0 NormalZ=1 AngleXU=0 Radius=10
    g13: Circle [constr] CenterX=14.5 CenterY=29 CenterZ=0 NormalX=0 NormalY=0 NormalZ=1 AngleXU=0 Radius=10
    g14: ArcOfCircle CenterX=34.3876 CenterY=39.0423 CenterZ=0 NormalX=0 NormalY=0 NormalZ=1 AngleXU=0 Radius=59.9083 StartAngle=3.34419 EndAngle=3.57406
    g15: ArcOfCircle CenterX=-14.5 CenterY=29 CenterZ=0 NormalX=0 NormalY=0 NormalZ=1 AngleXU=0 Radius=10 StartAngle=1.70851 EndAngle=3.34419
    g16: ArcOfCircle CenterX=76.5816 CenterY=58.5195 CenterZ=0 NormalX=0 NormalY=0 NormalZ=1 AngleXU=0 Radius=106.381 StartAngle=3.57406 EndAngle=3.79409
    g17: Circle [constr] CenterX=0 CenterY=0 CenterZ=0 NormalX=0 NormalY=0 NormalZ=1 AngleXU=0 Radius=10
    g18: ArcOfCircle CenterX=0 CenterY=0 CenterZ=0 NormalX=0 NormalY=0 NormalZ=1 AngleXU=0 Radius=10 StartAngle=3.79409 EndAngle=5.63069
    g19: ArcOfCircle CenterX=-34.3877 CenterY=39.0423 CenterZ=0 NormalX=0 NormalY=0 NormalZ=1 AngleXU=0 Radius=59.9085 StartAngle=5.85072 EndAngle=6.08059
    g20: ArcOfCircle CenterX=14.5 CenterY=29 CenterZ=0 NormalX=0 NormalY=0 NormalZ=1 AngleXU=0 Radius=10 StartAngle=6.08059 EndAngle=7.71627
    g21: ArcOfCircle CenterX=-76.5816 CenterY=58.5195 CenterZ=0 NormalX=0 NormalY=0 NormalZ=1 AngleXU=0 Radius=106.381 StartAngle=5.63069 EndAngle=5.85072
    g22: ArcOfCircle CenterX=0 CenterY=-75.6253 CenterZ=0 NormalX=0 NormalY=0 NormalZ=1 AngleXU=0 Radius=115.625 StartAngle=1.5708 EndAngle=1.70851
    g23: ArcOfCircle CenterX=0 CenterY=-75.6249 CenterZ=0 NormalX=0 NormalY=0 NormalZ=1 AngleXU=0 Radius=115.625 StartAngle=1.43308 EndAngle=1.5708
  constraints (64):
    c: PointOnObject(g13,g0)
    c: PointOnObject(g12,g0)
    c: Radius(g1) = 2.5
    c: PointOnObject(g12,g1)
    c: Equal(g2,g1)
    c: Tangent(g2,g0)
    c: Radius(g3) = 4
    c: Tangent(g4,g2) = -1.5708
    c: Tangent(g6,g1) = 1.5708
    c: Coincident(g7,g6)
    c: Coincident(g8,g2)
    c: Coincident(g8,g4)
    c: Coincident(g9,g3)
    c: Coincident(g5,g7)
    c: Coincident(g8,g5)
    c: Horizontal(g5)
    c: Vertical(g7,g5)
    c: Vertical(g8,g5)
    c: Vertical(g0,g9)
    c: Equal(g9,g3)
    c: Tangent(g9,g6) = 1.5708
    c: Tangent(g4,g9) = -1.5708
    c: Tangent(g5,g1) = 1.5708
    c: Tangent(g0,g7)
    c: PointOnObject(g10,g4)
    c: Distance(g10) = 10
    c: PointOnObject(g11,g6)
    c: Distance(g11) = 10
    c: Horizontal(g11,g0)
    c: Horizontal(g10,g0)
    c: Perpendicular(g6,g11)
    c: Perpendicular(g4,g10)
    c: PointOnObject(g22,g-2)
    c: Radius(g12) = 10
    c: Radius(g13) = 10
    c: Radius(g17) = 10
    c: Tangent(g16,g17) = -1.5708
    c: Coincident(g18,g16)
    c: Tangent(g21,g18) = -1.5708
    c: Tangent(g15,g14) = -1.5708
    c: Tangent(g19,g20) = -1.5708
    c: Tangent(g22,g15) = -1.5708
    c: PointOnObject(g14,g12)
    c: Tangent(g23,g20) = -1.5708
    c: PointOnObject(g19,g13)
    c: Coincident(g16,g11)
    c: Perpendicular(g16,g11)
    c: Tangent(g14,g16) = -1.5708
    c: Tangent(g19,g21) = -1.5708
    c: Coincident(g19,g10)
    c: Perpendicular(g21,g10)
    c: Tangent(g23,g22) = -1.5708
    c: Coincident(g-1,g18)
    c: Coincident(g17,g18)
    c: PointOnObject(g9,g-2)
    c: Coincident(g20,g13)
    c: Coincident(g15,g12)
    c: PointOnObject(g20,g8)
    c: PointOnObject(g18,g9)
    c: PointOnObject(g18,g0)
    c: Distance(g22,g5) = 10
    c: Distance(g18,g5) = 30
    c: Perpendicular(g22,g-2)
    c: DistanceX(g7,g8) = 25
FEATURE [PartDesign::Pad] Pad
  AllowMultiFace = false
  Direction = (0,0,1)
  Length = 12.8
  Length2 = 100
  Profile = -> Sketch
  Suppressed = false
  Type = 0
  expr: Length = Spreadsheet.CoilThickness
FEATURE [PartDesign::Body] Body  label="Stator_Coil"
  AllowCompound = false
  Group = -> [Sketch,Pad]
  Origin = -> Origin
  Tip = -> Pad
FEATURE [Spreadsheet::Sheet] Spreadsheet
  cells = A1='Inputs; A2='CoilHoleWidthAtOuterRadius; B2(CoilHoleWidthAtOuterRadius)==Master_of_Puppets#Spreadsheet.CoilHoleWidthAtOuterRadius; A3='CoilHoleWidthAtInnerRadius; B3(CoilHoleWidthAtInnerRadius)==Master_of_Puppets#Spreadsheet.CoilHoleWidthAtInnerRadius; A4='MagnetWidth; B4(MagnetWidth)==Master_of_Puppets#Spreadsheet.MagnetWidth; A5='MagnetLength; B5(MagnetLength)==Master_of_Puppets#Spreadsheet.MagnetLength; A6='CoilType; B6(CoilType)==Master_of_Puppets#Spreadsheet.CoilType; A7='SmallestMagnetDimension; B7(SmallestMagnetDimension)==Master_of_Puppets#Alternator.SmallestMagnetDimension; A8='CoilLegWidth; B8(CoilLegWidth)==CoilType != 3 ? SmallestMagnetDimension / 2 : Master_of_Puppets#Spreadsheet.CoilLegWidth; C8='Prevent this from breaking when not triangular coils; A9='CoilWinderPinRadius; B9(CoilWinderPinRadius)==Master_of_Puppets#Alternator.CoilWinderPinRadius; A10='CoilThickness; B10(CoilThickness)==Master_of_Puppets#Alternator.CoilThickness; A11='CoilLegWidthReduced; B11(CoilLegWidthReduced)==Master_of_Puppets#Alternator.CoilLegWidthReduced; A12='HorizontalDistanceBetweenPins; B12(HorizontalDistanceBetweenPins)==Master_of_Puppets#Alternator.TriangularHorizontalDistanceBetweenPins; A13='LargestMagnetDimension; B13(LargestMagnetDimension)==Master_of_Puppets#Alternator.LargestMagnetDimension; A14='Calculated; A15='CornerCircleRadius; B15(CornerCircleRadius)==CoilType != 3 ? CoilLegWidth : CoilLegWidthReduced; C15='Prevent this from breaking when not triangular coils; A16='InnerBottomArcRadius; B16(InnerBottomArcRadius)==CoilType == 3 ? CoilHoleWidthAtInnerRadius / 2 : 4; C16='Duplicated in Stator_Coil_Triangular_Reduced; A17='VerticalDimension; B17(VerticalDimension)==CoilType != 3 ? LargestMagnetDimension : MagnetLength; C17='Prevent this from breaking when not triangular coils
---- part Stator_CoilWinder_Cheek.FCStd = doc fcstd_5f320d548366 ----
FCSTD DOCUMENT  (FreeCAD 1.0R39109 (Git))
Label: Stator_CoilWinder_Cheek
Comment: Back Cheek
License: All rights reserved
LicenseURL: http://en.wikipedia.org/wiki/All_rights_reserved
objects: Sketcher::SketchObject×4, PartDesign::Pocket×3, TechDraw::DrawViewDimension×3, PartDesign::Mirrored×2, PartDesign::Pad×1, Spreadsheet::Sheet×1, PartDesign::Body×1, TechDraw::DrawSVGTemplate×1, TechDraw::DrawProjGroupItem×1, TechDraw::DrawPage×1
note: 31 computed .brp shape members not serialized (recipe doc carries the construction recipe); baked Part::Feature solids carry a one-line shape summary decoded from their .brp
EXTERNAL_REF file=../../../Master_of_Puppets.FCStd obj=Alternator
EXTERNAL_REF file=../../../Master_of_Puppets.FCStd obj=Spreadsheet

FEATURE [Sketcher::SketchObject] Sketch
  ArcFitTolerance = 0
  AttachmentSupport = -> [XY_Plane001]
  FullyConstrained = true
  MakeInternals = false
  MapMode = 5
  expr: Constraints[1] = Spreadsheet.CoilWinderDiskRadius
  sketch-geometry (1):
    g0: Circle CenterX=0 CenterY=0 CenterZ=0 NormalX=0 NormalY=0 NormalZ=1 AngleXU=0 Radius=60.9591
  constraints (2):
    c: Coincident(g0,g-1)
    c: Radius(g0) = 60.9591
FEATURE [PartDesign::Pad] Pad
  AllowMultiFace = false
  Direction = (0,0,1)
  Length = 12
  Length2 = 100
  Profile = -> Sketch
  Suppressed = false
  Type = 0
  expr: Length = Spreadsheet.CoilWinderCheekThickness
FEATURE [Sketcher::SketchObject] Sketch001  label="CenterHoleSketch"
  ArcFitTolerance = 0
  AttachmentSupport = -> [XY_Plane001]
  FullyConstrained = true
  MakeInternals = false
  MapMode = 5
  Placement = pos=(0,0,0) rot=(0,1,0;3.14159rad)
  expr: Constraints[1] = Spreadsheet.CoilWinderCenterRodRadius
  sketch-geometry (1):
    g0: Circle CenterX=0 CenterY=0 CenterZ=0 NormalX=0 NormalY=0 NormalZ=1 AngleXU=0 Radius=5
  constraints (2):
    c: Coincident(g0,g-1)
    c: Radius(g0) = 5
FEATURE [PartDesign::Pocket] Pocket  label="CenterHolePocket"
  AllowMultiFace = false
  BaseFeature = -> Pad
  Direction = (0,0,1)
  Length = 5
  Length2 = 100
  Profile = -> Sketch001
  Suppressed = false
  Type = 1
FEATURE [Sketcher::SketchObject] Sketch002  label="PinHolesSketch"
  ArcFitTolerance = 0
  AttachmentSupport = -> [XY_Plane001]
  FullyConstrained = true
  MakeInternals = false
  MapMode = 5
  Placement = pos=(0,0,0) rot=(0,1,0;3.14159rad)
  expr: Constraints[0] = Spreadsheet.CoilWinderPinRadius
  expr: Constraints[1] = Spreadsheet.RectangularVerticalDistanceOfHolesFromCenter
  expr: Constraints[2] = Spreadsheet.OuterHorizontalDistanceFromCenter
  expr: Constraints[4] = Spreadsheet.RectangularVerticalDistanceOfHolesFromCenter
  expr: Constraints[5] = Spreadsheet.InnerHorizontalDistanceFromCenter
  sketch-geometry (2):
    g0: Circle CenterX=12.5 CenterY=20.5 CenterZ=0 NormalX=0 NormalY=0 NormalZ=1 AngleXU=0 Radius=2.5
    g1: Circle CenterX=12.5 CenterY=-20.5 CenterZ=0 NormalX=0 NormalY=0 NormalZ=1 AngleXU=0 Radius=2.5
  constraints (6):
    c: Radius(g0) = 2.5
    c: DistanceY(g-1,g0) = 20.5
    c: DistanceX(g-1,g0) = 12.5
    c: Equal(g0,g1)
    c: DistanceY(g1,g-1) = 20.5
    c: DistanceX(g-1,g1) = 12.5
FEATURE [Spreadsheet::Sheet] Spreadsheet
  cells = A1='Inputs; A2='Spreadsheet; A3='MagnetWidth; B3(MagnetWidth)==Master_of_Puppets#Spreadsheet.MagnetWidth; A4='MagnetLength; B4(MagnetLength)==Master_of_Puppets#Spreadsheet.MagnetLength; A5='CoilHoleWidthAtOuterRadius; B5(CoilHoleWidthAtOuterRadius)==Master_of_Puppets#Spreadsheet.CoilHoleWidthAtOuterRadius; A6='CoilHoleWidthAtInnerRadius; B6(CoilHoleWidthAtInnerRadius)==Master_of_Puppets#Spreadsheet.CoilHoleWidthAtInnerRadius; A7='CoilType; B7(CoilType)==Master_of_Puppets#Spreadsheet.CoilType; A8='Alternator; A9='CoilWinderDiskRadius; B9(CoilWinderDiskRadius)==Master_of_Puppets#Alternator.CoilWinderDiskRadius; A10='CoilWinderCenterRodRadius; B10(CoilWinderCenterRodRadius)==Master_of_Puppets#Alternator.CoilWinderCenterRodRadius; A11='CoilWinderPinRadius; B11(CoilWinderPinRadius)==Master_of_Puppets#Alternator.CoilWinderPinRadius; A12='CoilWinderDiskTapeNotchWidth; B12(CoilWinderDiskTapeNotchWidth)==Master_of_Puppets#Alternator.CoilWinderDiskTapeNotchWidth; A13='CoilWinderDiskFillet; B13(CoilWinderDiskFillet)==Master_of_Puppets#Alternator.CoilWinderDiskFillet; A14='RectangularVerticalDistanceOfHolesFromCenter; B14(RectangularVerticalDistanceOfHolesFromCenter)==Master_of_Puppets#Alternator.RectangularVerticalDistanceOfHolesFromCenter; A15='CoilWinderCheekThickness; B15(CoilWinderCheekThickness)==Master_of_Puppets#Alternator.CoilWinderCheekThickness; A16='OuterHorizontalDistanceBetweenCenterOfSmallHoles; B16(OuterHorizontalDistanceBetweenCenterOfSmallHoles)==Master_of_Puppets#Alternator.OuterHorizontalDistanceBetweenCenterOfSmallHoles; A17='InnerHorizontalDistanceBetweenCenterOfSmallHoles; B17(InnerHorizontalDistanceBetweenCenterOfSmallHoles)==Master_of_Puppets#Alternator.InnerHorizontalDistanceBetweenCenterOfSmallHoles; A18='Calculated; A19='CoilWinderDiskSmallHoleDiameter; B19(CoilWinderDiskSmallHoleDiameter)==CoilWinderPinRadius * 2; A20='OuterHorizontalDistanceFromCenter; B20(OuterHorizontalDistanceFromCenter)==OuterHorizontalDistanceBetweenCenterOfSmallHoles / 2; A21='InnerHorizontalDistanceFromCenter; B21(InnerHorizontalDistanceFromCenter)==InnerHorizontalDistanceBetweenCenterOfSmallHoles / 2; A22='SmallestOuterDimension; B22(SmallestOuterDimension)==min(CoilHoleWidthAtOuterRadius; MagnetLength); A23='TapeNotchOuterDistanceFromCenter; B23(TapeNotchOuterDistanceFromCenter)==(SmallestOuterDimension - CoilWinderDiskSmallHoleDiameter) / 2; A24='SmallestInnerDimension; B24(SmallestInnerDimension)==min(CoilHoleWidthAtInnerRadius; MagnetLength); A25='TapeNotchInnerDistanceFromCenter; B25(TapeNotchInnerDistanceFromCenter)==CoilType != 3 ? (SmallestInnerDimension - CoilWinderDiskSmallHoleDiameter) / 2 : TapeNotchOuterDistanceFromCenter
FEATURE [Sketcher::SketchObject] Sketch005  label="TapeNotchSketch"
  ArcFitTolerance = 0
  AttachmentSupport = -> [XY_Plane001]
  FullyConstrained = true
  MakeInternals = false
  MapMode = 5
  Placement = pos=(0,0,0) rot=(0,1,0;3.14159rad)
  expr: Constraints[13] = Spreadsheet.CoilWinderDiskFillet
  expr: Constraints[17] = Spreadsheet.CoilWinderDiskFillet
  expr: Constraints[23] = Spreadsheet.OuterHorizontalDistanceFromCenter
  expr: Constraints[24] = Spreadsheet.InnerHorizontalDistanceFromCenter
  expr: Constraints[25] = Spreadsheet.RectangularVerticalDistanceOfHolesFromCenter * 2
  expr: Constraints[26] = Spreadsheet.RectangularVerticalDistanceOfHolesFromCenter
  expr: Constraints[7] = Spreadsheet.CoilWinderDiskTapeNotchWidth
  expr: Constraints[9] = Spreadsheet.CoilWinderDiskRadius
  sketch-geometry (10):
    g0: LineSegment StartX=12.5 StartY=10.5 StartZ=0 EndX=49.6227 EndY=10.5 EndZ=0
    g1: LineSegment StartX=12.5 StartY=-10.5 StartZ=0 EndX=49.6227 EndY=-10.5 EndZ=0
    g2: GeomPoint [constr] X=12.5 Y=0 Z=0
    g3: LineSegment StartX=12.5 StartY=10.5 StartZ=0 EndX=12.5 EndY=0 EndZ=0
    g4: LineSegment StartX=12.5 StartY=0 StartZ=0 EndX=12.5 EndY=-10.5 EndZ=0
    g5: Circle [constr] CenterX=0 CenterY=0 CenterZ=0 NormalX=0 NormalY=0 NormalZ=1 AngleXU=0 Radius=60.9591
    g6: ArcOfCircle CenterX=0 CenterY=0 CenterZ=0 NormalX=0 NormalY=0 NormalZ=1 AngleXU=0 Radius=60.9591 StartAngle=5.92633 EndAngle=6.64004
    g7: ArcOfCircle CenterX=49.6227 CenterY=18.5 CenterZ=0 NormalX=0 NormalY=0 NormalZ=1 AngleXU=0 Radius=8 StartAngle=4.71239 EndAngle=6.64003
    g8: ArcOfCircle CenterX=49.6227 CenterY=-18.5 CenterZ=0 NormalX=0 NormalY=0 NormalZ=1 AngleXU=0 Radius=8 StartAngle=5.92633 EndAngle=7.85398
    g9: LineSegment [constr] StartX=12.5 StartY=-20.5 StartZ=0 EndX=12.5 EndY=20.5 EndZ=0
  constraints (27):
    c: Parallel(g1,g0)
    c: Coincident(g3,g0)
    c: Coincident(g3,g2)
    c: Coincident(g4,g3)
    c: Coincident(g4,g1)
    c: Equal(g3,g4)
    c: Perpendicular(g3,g0)
    c: Distance(g1,g0) = 21
    c: Coincident(g5,g-1)
    c: Radius(g5) = 60.9591
    c: PointOnObject(g6,g5)
    c: Coincident(g6,g5)
    c: Tangent(g0,g7) = -1.5708
    c: Radius(g7) = 8
    c: Coincident(g6,g7)
    c: Tangent(g7,g5)
    c: Tangent(g1,g8) = 1.5708
    c: Radius(g8) = 8
    c: Tangent(g6,g8) = -1.5708
    c: PointOnObject(g1,g9)
    c: PointOnObject(g0,g9)
    c: PointOnObject(g2,g9)
    c: PointOnObject(g2,g-1)
    c: DistanceX(g9) = 12.5
    c: DistanceX(g-1,g9) = 12.5
    c: DistanceY(g9,g9) = 41
    c: DistanceY(g-1,g9) = 20.5
FEATURE [PartDesign::Pocket] Pocket005  label="PinHolesPocket"
  BaseFeature = -> Pocket
  Direction = (0,0,1)
  Length = 5
  Length2 = 5
  Profile = -> Sketch002
  ReferenceAxis = -> Sketch002 [N_Axis]
  Suppressed = false
  Type = 1
FEATURE [PartDesign::Mirrored] Mirrored001  label="PinHolesPocketMirrorred"
  BaseFeature = -> Pocket005
  MirrorPlane = -> Sketch002 [V_Axis]
  Originals = -> [Pocket005]
  Suppressed = false
  TransformMode = 0
FEATURE [PartDesign::Pocket] Pocket004  label="TapeNotchPocket"
  AllowMultiFace = false
  BaseFeature = -> Mirrored001
  Direction = (0,0,1)
  Length = 5
  Length2 = 100
  Profile = -> Sketch005
  Suppressed = false
  Type = 1
FEATURE [PartDesign::Mirrored] Mirrored  label="TapeNotchPocketMirrored"
  BaseFeature = -> Pocket004
  MirrorPlane = -> Sketch005 [V_Axis]
  Originals = -> [Pocket004]
  Suppressed = false
  TransformMode = 0
FEATURE [PartDesign::Body] PolarPattern001Body  label="Stator_CoilWinder_Cheek"
  AllowCompound = false
  Group = -> [Sketch,Pad,Sketch001,Pocket,Pocket005,Mirrored001,Sketch002,Sketch005,Pocket004,Mirrored]
  Openafpm_Flat = true
  Origin = -> Origin001
  Tip = -> Mirrored
FEATURE [TechDraw::DrawSVGTemplate] Template
  Height = 210
  Orientation = 1
  Template = <userpath>/micromamba/envs/openafpm-cad-core/share/Mod/TechDraw/Templates/Default_Template_A4_Landscape.svg
  Width = 297
FEATURE [TechDraw::DrawProjGroupItem] View
  CoarseView = false
  Direction = (0,0,1)
  Focus = 100
  HardHidden = false
  IsoCount = 0
  IsoHidden = false
  IsoVisible = false
  LockPosition = false
  Perspective = false
  Rotation = 0
  RotationVector = (1,0,0)
  ScaleType = 0
  ScrubCount = 1
  SeamHidden = false
  SeamVisible = false
  SmoothHidden = false
  SmoothVisible = true
  Source = -> [PolarPattern001Body]
  Type = 0
  X = 132.704
  XDirection = (1,0,0)
  Y = 103.638
FEATURE [TechDraw::DrawViewDimension] Dimension  label="A"
  AngleOverride = false
  Arbitrary = true
  ArbitraryTolerances = false
  BoxCorners = (2) [(-57.6227,-60.9591,0),(57.6227,60.9591,0)]
  EqualTolerance = true
  ExtensionAngle = 0
  FormatSpec = A
  FormatSpecOverTolerance = %+.2w
  FormatSpecUnderTolerance = %+.2w
  Inverted = false
  LineAngle = 0
  LockPosition = false
  MeasureType = 1
  OverTolerance = 0
  References2D = -> [View]
  Rotation = 0
  ScaleType = 0
  TheoreticalExact = false
  Type = 2
  UnderTolerance = 0
  X = -75.1271
  Y = 0
FEATURE [TechDraw::DrawViewDimension] Dimension001  label="B"
  AngleOverride = false
  Arbitrary = true
  ArbitraryTolerances = false
  BoxCorners = (2) [(-57.6227,-60.9591,0),(57.6227,60.9591,0)]
  EqualTolerance = true
  ExtensionAngle = 0
  FormatSpec = B
  FormatSpecOverTolerance = %+.2w
  FormatSpecUnderTolerance = %+.2w
  Inverted = false
  LineAngle = 0
  LockPosition = false
  MeasureType = 1
  OverTolerance = 0
  References2D = -> [View]
  Rotation = 0
  ScaleType = 0
  TheoreticalExact = false
  Type = 1
  UnderTolerance = 0
  X = 0
  Y = 73.3273
FEATURE [TechDraw::DrawViewDimension] Dimension002  label="C"
  AngleOverride = false
  Arbitrary = true
  ArbitraryTolerances = false
  BoxCorners = (2) [(-57.6227,-60.9591,0),(57.6227,60.9591,0)]
  EqualTolerance = true
  ExtensionAngle = 0
  FormatSpec = C
  FormatSpecOverTolerance = %+.2w
  FormatSpecUnderTolerance = %+.2w
  Inverted = false
  LineAngle = 0
  LockPosition = false
  MeasureType = 1
  OverTolerance = 0
  References2D = -> [View]
  Rotation = 0
  ScaleType = 0
  TheoreticalExact = false
  Type = 1
  UnderTolerance = 0
  X = 0
  Y = -67.5663
FEATURE [TechDraw::DrawPage] Page
  KeepUpdated = true
  NextBalloonIndex = 1
  ProjectionType = 0
  Template = -> Template
  Views = -> [View,Dimension,Dimension001,Dimension002]
---- part Stator_CoilWinder_Cheek_Notch.FCStd = doc fcstd_d5bdacb53a94 ----
FCSTD DOCUMENT  (FreeCAD 1.0R39109 (Git))
Label: Stator_CoilWinder_Cheek_Notch
Comment: Front Cheek
License: All rights reserved
LicenseURL: http://en.wikipedia.org/wiki/All_rights_reserved
objects: Spreadsheet::Sheet×1, Sketcher::SketchObject×1, App::Link×1, PartDesign::SubShapeBinder×1, PartDesign::FeatureBase×1, PartDesign::Pocket×1, PartDesign::Mirrored×1, PartDesign::Body×1
note: 11 computed .brp shape members not serialized (recipe doc carries the construction recipe); baked Part::Feature solids carry a one-line shape summary decoded from their .brp
EXTERNAL_REF file=../../../Master_of_Puppets.FCStd obj=Alternator
EXTERNAL_REF file=../../../Master_of_Puppets.FCStd obj=Spreadsheet
EXTERNAL_REF file=Stator_CoilWinder_Cheek.FCStd obj=PolarPattern001Body
EXTERNAL_REF file=Stator_CoilWinder_Cheek_Triangular.FCStd obj=PolarPattern001Body

FEATURE [Spreadsheet::Sheet] Spreadsheet
  cells = A1='Inputs; A2='Spreadsheet; A3='MagnetLength; B3(MagnetLength)==Master_of_Puppets#Spreadsheet.MagnetLength; A4='CoilType; B4(CoilType)==Master_of_Puppets#Spreadsheet.CoilType; A5='CoilHoleWidthAtOuterRadius; B5(CoilHoleWidthAtOuterRadius)==Master_of_Puppets#Spreadsheet.CoilHoleWidthAtOuterRadius; A6='RectangularVerticalDistanceOfHolesFromCenter; B6(RectangularLargestDistanceOfHolesFromCenter)==Master_of_Puppets#Alternator.RectangularVerticalDistanceOfHolesFromCenter; A7='Alternator; A8='CoilWinderDiskRadius; B8(CoilWinderDiskRadius)==Master_of_Puppets#Alternator.CoilWinderDiskRadius; A9='CoilWinderPinRadius; B9(CoilWinderPinRadius)==Master_of_Puppets#Alternator.CoilWinderPinRadius; A10='CoilWinderDiskFillet; B10(CoilWinderDiskFillet)==Master_of_Puppets#Alternator.CoilWinderDiskFillet; A11='TriangularCoilWinderCircumradius; B11(TriangularCoilWinderCircumradius)==Master_of_Puppets#Alternator.TriangularCoilWinderCircumradius; A12='TriangularVerticalDistanceOfHolesFromCenter; B12(TriangularVerticalDistanceOfHolesFromCenter)==Master_of_Puppets#Alternator.TriangularVerticalDistanceOfHolesFromCenter; C12='With respect to center of holes; A13='Static; A14='NotchAngle; B14(NotchAngle)=50; A15='Calculated; A16='Stator_CoilWinder_Cheek; B16(Stator_CoilWinder_Cheek)==CoilType != 3 ? <<Stator_CoilWinder_Cheek>>#<<Stator_CoilWinder_Cheek>>._self : <<Stator_CoilWinder_Cheek_Triangular>>#<<Stator_CoilWinder_Cheek>>._self; A17='DistanceOfNotchFromCenter; B17(DistanceOfNotchFromCenter)==(CoilType != 3 ? RectangularLargestDistanceOfHolesFromCenter : TriangularVerticalDistanceOfHolesFromCenter) + CoilWinderPinRadius
FEATURE [Sketcher::SketchObject] Sketch004  label="NotchSketch"
  ArcFitTolerance = 0
  AttachmentSupport = -> [XY_Plane001]
  FullyConstrained = true
  MakeInternals = false
  MapMode = 5
  Placement = pos=(0,0,0) rot=(0,1,0;3.14159rad)
  expr: Constraints[11] = Spreadsheet.NotchAngle / 2
  expr: Constraints[1] = Spreadsheet.DistanceOfNotchFromCenter
  expr: Constraints[3] = Spreadsheet.CoilWinderDiskRadius
  expr: Constraints[5] = Spreadsheet.CoilWinderDiskFillet
  expr: Constraints[6] = Spreadsheet.CoilWinderDiskRadius
  sketch-geometry (5):
    g0: Circle [constr] CenterX=0 CenterY=0 CenterZ=0 NormalX=0 NormalY=0 NormalZ=1 AngleXU=0 Radius=60.4591
    g1: LineSegment StartX=0 StartY=15 StartZ=0 EndX=-16.4152 EndY=50.2025 EndZ=0
    g2: ArcOfCircle CenterX=-23.6656 CenterY=46.8215 CenterZ=0 NormalX=0 NormalY=0 NormalZ=1 AngleXU=0 Radius=8 StartAngle=0.436332 EndAngle=2.00713
    g3: ArcOfCircle CenterX=-1.49549 CenterY=-0.722529 CenterZ=0 NormalX=0 NormalY=0 NormalZ=1 AngleXU=0 Radius=60.4591 StartAngle=1.54606 EndAngle=2.00713
    g4: LineSegment StartX=0 StartY=15 StartZ=0 EndX=0 EndY=59.718 EndZ=0
  constraints (14):
    c: PointOnObject(g1,g-2)
    c: DistanceY(g-1,g1) = 15
    c: Coincident(g0,g-1)
    c: Radius(g0) = 60.4591
    c: Tangent(g1,g2) = -1.5708
    c: Radius(g2) = 8
    c: Radius(g3) = 60.4591
    c: Angle(g2) = 1.5708
    c: Coincident(g4,g1)
    c: Coincident(g4,g3)
    c: Vertical(g4)
    c: Angle(g4,g1) = 0.436332
    c: PointOnObject(g2,g0)
    c: Tangent(g2,g3) = -1.5708
FEATURE [App::Link] Link  label="Stator_CoilWinder_Cheek"
  LinkedObject = -> <external Stator_CoilWinder_Cheek.FCStd>#PolarPattern001Body
  expr: LinkedObject = Spreadsheet.Stator_CoilWinder_Cheek
FEATURE [PartDesign::SubShapeBinder] Binder
  BindCopyOnChange = 0
  BindMode = 0
  ClaimChildren = true
  Context = -> PolarPattern001Body [Binder.]
  Fuse = false
  MakeFace = true
  OffsetFill = false
  OffsetIntersection = false
  OffsetJoinType = 0
  OffsetOpenResult = false
  PartialLoad = false
  Refine = true
  Relative = true
  Support = -> [Link]
  _Version = 2
FEATURE [PartDesign::FeatureBase] BaseFeature
  BaseFeature = -> Binder
  Suppressed = false
FEATURE [PartDesign::Pocket] Pocket  label="NotchPocket"
  BaseFeature = -> BaseFeature
  Direction = (0,0,1)
  Length = 5
  Length2 = 100
  Profile = -> Sketch004
  Suppressed = false
  Type = 1
FEATURE [PartDesign::Mirrored] Mirrored
  BaseFeature = -> Pocket
  MirrorPlane = -> Sketch004 [V_Axis]
  Originals = -> [Pocket]
  Suppressed = false
  TransformMode = 0
FEATURE [PartDesign::Body] PolarPattern001Body  label="Stator_CoilWinder_Cheek_Notch"
  AllowCompound = false
  BaseFeature = -> Binder
  Group = -> [BaseFeature,Sketch004,Binder,Pocket,Mirrored]
  Openafpm_Flat = true
  Origin = -> Origin001
  Tip = -> Mirrored
---- part Stator_CoilWinder_Cheek_Triangular.FCStd = doc fcstd_0f03d15e17e1 ----
FCSTD DOCUMENT  (FreeCAD 1.0R39109 (Git))
Label: Stator_CoilWinder_Cheek_Triangular
Comment: Back Cheek
License: All rights reserved
LicenseURL: http://en.wikipedia.org/wiki/All_rights_reserved
objects: Sketcher::SketchObject×4, PartDesign::Pocket×3, TechDraw::DrawViewDimension×3, PartDesign::Pad×1, Spreadsheet::Sheet×1, PartDesign::Mirrored×1, PartDesign::Body×1, TechDraw::DrawSVGTemplate×1, TechDraw::DrawProjGroupItem×1, TechDraw::DrawPage×1
note: 28 computed .brp shape members not serialized (recipe doc carries the construction recipe); baked Part::Feature solids carry a one-line shape summary decoded from their .brp
EXTERNAL_REF file=../../../Master_of_Puppets.FCStd obj=Alternator
EXTERNAL_REF file=../../../Master_of_Puppets.FCStd obj=Spreadsheet

FEATURE [Sketcher::SketchObject] Sketch
  ArcFitTolerance = 0
  AttachmentSupport = -> [XY_Plane001]
  FullyConstrained = true
  MakeInternals = false
  MapMode = 5
  expr: Constraints[1] = Spreadsheet.CoilWinderDiskRadius
  sketch-geometry (1):
    g0: Circle CenterX=0 CenterY=0 CenterZ=0 NormalX=0 NormalY=0 NormalZ=1 AngleXU=0 Radius=69.3453
  constraints (2):
    c: Coincident(g0,g-1)
    c: Radius(g0) = 69.3453
FEATURE [PartDesign::Pad] Pad
  AllowMultiFace = false
  Direction = (0,0,1)
  Length = 12
  Length2 = 100
  Profile = -> Sketch
  Suppressed = false
  Type = 0
  expr: Length = Spreadsheet.CoilWinderCheekThickness
FEATURE [Sketcher::SketchObject] Sketch001  label="CenterHoleSketch"
  ArcFitTolerance = 0
  AttachmentSupport = -> [XY_Plane001]
  FullyConstrained = true
  MakeInternals = false
  MapMode = 5
  Placement = pos=(0,0,0) rot=(0,1,0;3.14159rad)
  expr: Constraints[1] = Spreadsheet.CoilWinderCenterRodRadius
  sketch-geometry (1):
    g0: Circle CenterX=0 CenterY=0 CenterZ=0 NormalX=0 NormalY=0 NormalZ=1 AngleXU=0 Radius=5
  constraints (2):
    c: Coincident(g0,g-1)
    c: Radius(g0) = 5
FEATURE [PartDesign::Pocket] Pocket  label="CenterHolePocket"
  AllowMultiFace = false
  BaseFeature = -> Pad
  Direction = (0,0,1)
  Length = 5
  Length2 = 100
  Profile = -> Sketch001
  Suppressed = false
  Type = 1
FEATURE [Spreadsheet::Sheet] Spreadsheet
  cells = A1='Inputs; A2='Spreadsheet; A3='CoilHoleWidthAtInnerRadius; B3(CoilHoleWidthAtInnerRadius)==Master_of_Puppets#Spreadsheet.CoilHoleWidthAtInnerRadius; A4='CoilType; B4(CoilType)==Master_of_Puppets#Spreadsheet.CoilType; A5='MagnetWidth; B5(MagnetWidth)==Master_of_Puppets#Spreadsheet.MagnetWidth; A6='MagnetLength; B6(MagnetLength)==Master_of_Puppets#Spreadsheet.MagnetLength; A7='Alternator; A8='CoilWinderDiskRadius; B8(CoilWinderDiskRadius)==Master_of_Puppets#Alternator.CoilWinderDiskRadius; A9='CoilWinderCenterRodRadius; B9(CoilWinderCenterRodRadius)==Master_of_Puppets#Alternator.CoilWinderCenterRodRadius; A10='CoilWinderPinRadius; B10(CoilWinderPinRadius)==Master_of_Puppets#Alternator.CoilWinderPinRadius; A11='CoilWinderDiskTapeNotchWidth; B11(CoilWinderDiskTapeNotchWidth)==Master_of_Puppets#Alternator.CoilWinderDiskTapeNotchWidth; A12='CoilWinderDiskFillet; B12(CoilWinderDiskFillet)==Master_of_Puppets#Alternator.CoilWinderDiskFillet; A13='BottomHoleRadius; B13(BottomHoleRadius)==Master_of_Puppets#Alternator.CoilWinderDiskBottomHoleRadius; A14='CoilWinderCheekThickness; B14(CoilWinderCheekThickness)==Master_of_Puppets#Alternator.CoilWinderCheekThickness; A15='DistanceBetweenTriangularCoilAndTapeNotch; B15(DistanceBetweenTriangularCoilAndTapeNotch)==Master_of_Puppets#Alternator.DistanceBetweenTriangularCoilAndTapeNotch
FEATURE [Sketcher::SketchObject] Sketch006  label="HolesSketch"
  ArcFitTolerance = 0
  AttachmentSupport = -> [XY_Plane001]
  FullyConstrained = true
  MakeInternals = false
  MapMode = 5
  Placement = pos=(0,0,0) rot=(0,1,0;3.14159rad)
  expr: Constraints[16] = Spreadsheet.MagnetWidth
  expr: Constraints[18] = Spreadsheet.MagnetLength - Spreadsheet.BottomHoleRadius
  expr: Constraints[2] = Spreadsheet.BottomHoleRadius
  expr: Constraints[7] = Spreadsheet.CoilWinderPinRadius
  sketch-geometry (6):
    g0: Circle [constr] CenterX=0 CenterY=0 CenterZ=0 NormalX=0 NormalY=0 NormalZ=1 AngleXU=0 Radius=30.625
    g1: Circle CenterX=0 CenterY=-26.625 CenterZ=0 NormalX=0 NormalY=0 NormalZ=1 AngleXU=0 Radius=4
    g2: Circle CenterX=-22.5 CenterY=16.875 CenterZ=0 NormalX=0 NormalY=0 NormalZ=1 AngleXU=0 Radius=2.5
    g3: Circle CenterX=22.5 CenterY=16.875 CenterZ=0 NormalX=0 NormalY=0 NormalZ=1 AngleXU=0 Radius=2.5
    g4: ArcOfCircle [constr] CenterX=-22.5 CenterY=16.875 CenterZ=0 NormalX=0 NormalY=0 NormalZ=1 AngleXU=0 Radius=2.5 StartAngle=1.5708 EndAngle=3.14159
    g5: ArcOfCircle [constr] CenterX=22.5 CenterY=16.875 CenterZ=0 NormalX=0 NormalY=0 NormalZ=1 AngleXU=0 Radius=2.5 StartAngle=0 EndAngle=1.5708
  constraints (19):
    c: Coincident(g0,g-1)
    c: PointOnObject(g1,g-2)
    c: Radius(g1) = 4
    c: Equal(g3,g2)
    c: Horizontal(g2,g3)
    c: Tangent(g2,g0)
    c: Tangent(g3,g0)
    c: Radius(g2) = 2.5
    c: Coincident(g4,g2)
    c: PointOnObject(g4,g2)
    c: Horizontal(g4,g2)
    c: Vertical(g4,g2)
    c: Coincident(g5,g3)
    c: PointOnObject(g5,g3)
    c: Horizontal(g3,g5)
    c: Vertical(g3,g5)
    c: DistanceX(g4,g5) = 50
    c: Tangent(g1,g0)
    c: DistanceY(g1,g4) = 46
FEATURE [PartDesign::Pocket] Pocket001  label="HolesPocket"
  BaseFeature = -> Pocket
  Direction = (0,0,1)
  Length = 5
  Length2 = 100
  Profile = -> Sketch006
  Suppressed = false
  Type = 1
FEATURE [Sketcher::SketchObject] Sketch007  label="TapeNotchSketch"
  ArcFitTolerance = 0
  AttachmentOffset = pos=(0,0,12) rot=(0,0,1;0rad)
  AttachmentSupport = -> [XY_Plane001]
  ExternalGeometry = -> [Sketch006]
  FullyConstrained = true
  MakeInternals = false
  MapMode = 2
  Placement = pos=(0,0,12) rot=(0,0,1;0rad)
  expr: .AttachmentOffset.Base.z = Spreadsheet.CoilWinderCheekThickness
  expr: Constraints[0] = Spreadsheet.BottomHoleRadius
  expr: Constraints[10] = Spreadsheet.CoilWinderDiskRadius
  expr: Constraints[12] = Spreadsheet.CoilWinderDiskFillet
  expr: Constraints[16] = Spreadsheet.CoilWinderDiskFillet
  expr: Constraints[1] = Spreadsheet.CoilWinderPinRadius
  expr: Constraints[26] = Spreadsheet.DistanceBetweenTriangularCoilAndTapeNotch
  expr: Constraints[28] = Spreadsheet.DistanceBetweenTriangularCoilAndTapeNotch
  expr: Constraints[2] = Spreadsheet.CoilWinderDiskTapeNotchWidth
  sketch-geometry (11):
    g0: LineSegment [constr] StartX=0 StartY=-26.625 StartZ=0 EndX=3.60749 EndY=-28.353 EndZ=0
    g1: LineSegment [constr] StartX=22.5 StartY=16.875 StartZ=0 EndX=24.7547 EndY=15.795 EndZ=0
    g2: LineSegment StartX=7.84131 StartY=-14.8847 StartZ=0 EndX=16.9134 EndY=4.05465 EndZ=0
    g3: LineSegment StartX=7.84131 StartY=-14.8847 StartZ=0 EndX=48.5444 EndY=-34.3817 EndZ=0
    g4: LineSegment StartX=16.9134 StartY=4.05465 StartZ=0 EndX=57.3521 EndY=-15.3158 EndZ=0
    g5: Circle [constr] CenterX=0 CenterY=0 CenterZ=0 NormalX=0 NormalY=0 NormalZ=1 AngleXU=0 Radius=69.3453
    g6: ArcOfCircle CenterX=60.8081 CenterY=-8.10079 CenterZ=0 NormalX=0 NormalY=0 NormalZ=1 AngleXU=0 Radius=8 StartAngle=4.26568 EndAngle=6.15075
    g7: ArcOfCircle CenterX=-5.368e-13 CenterY=3e-13 CenterZ=0 NormalX=0 NormalY=0 NormalZ=1 AngleXU=0 Radius=69.3453 StartAngle=5.53805 EndAngle=6.15075
    g8: ArcOfCircle CenterX=45.0884 CenterY=-41.5967 CenterZ=0 NormalX=0 NormalY=0 NormalZ=1 AngleXU=0 Radius=8 StartAngle=5.53805 EndAngle=7.40727
    g9: LineSegment [constr] StartX=24.7547 StartY=15.795 StartZ=0 EndX=18.7171 EndY=3.19065 EndZ=0
    g10: LineSegment [constr] StartX=9.64505 StartY=-15.7487 StartZ=0 EndX=3.60749 EndY=-28.353 EndZ=0
  constraints (30):
    c: Distance(g0) = 4
    c: Distance(g1) = 2.5
    c: Distance(g2) = 21
    c: Coincident(g3,g2)
    c: Coincident(g4,g2)
    c: Parallel(g4,g3)
    c: Perpendicular(g2,g4)
    c: Coincident(g1,g-4)
    c: Coincident(g0,g-3)
    c: Coincident(g5,g-1)
    c: Radius(g5) = 69.3453
    c: Tangent(g4,g6) = -1.5708
    c: Radius(g6) = 8
    c: PointOnObject(g6,g5)
    c: Tangent(g7,g6) = -1.5708
    c: Tangent(g8,g3) = 1.5708
    c: Radius(g8) = 8
    c: Tangent(g8,g7) = -1.5708
    c: Tangent(g7,g5) = -1.5708
    c: Coincident(g9,g1)
    c: PointOnObject(g9,g4)
    c: PointOnObject(g10,g3)
    c: Coincident(g10,g0)
    c: Perpendicular(g0,g10)
    c: Perpendicular(g10,g3)
    c: Perpendicular(g4,g9)
    c: Distance(g9,g2) = 2
    c: Equal(g10,g9)
    c: Distance(g10,g2) = 2
    c: Perpendicular(g9,g1)
FEATURE [PartDesign::Pocket] Pocket002  label="TapeNotchPocket"
  BaseFeature = -> Pocket001
  Direction = (0,0,-1)
  Length = 5
  Length2 = 100
  Profile = -> Sketch007
  Suppressed = false
  Type = 1
FEATURE [PartDesign::Mirrored] Mirrored
  BaseFeature = -> Pocket002
  MirrorPlane = -> Sketch007 [V_Axis]
  Originals = -> [Pocket002]
  Suppressed = false
  TransformMode = 0
FEATURE [PartDesign::Body] PolarPattern001Body  label="Stator_CoilWinder_Cheek"
  AllowCompound = false
  Group = -> [Sketch,Pad,Sketch001,Pocket,Sketch006,Pocket001,Sketch007,Pocket002,Mirrored]
  Openafpm_Flat = true
  Origin = -> Origin001
  Tip = -> Mirrored
FEATURE [TechDraw::DrawSVGTemplate] Template
  Height = 210
  Orientation = 1
  Template = <userpath>/micromamba/envs/openafpm-cad-core/share/Mod/TechDraw/Templates/Default_Template_A4_Landscape.svg
  Width = 297
FEATURE [TechDraw::DrawProjGroupItem] View
  CoarseView = false
  Direction = (0,0,1)
  Focus = 100
  HardHidden = false
  IsoCount = 0
  IsoHidden = false
  IsoVisible = false
  LockPosition = false
  Perspective = false
  Rotation = 0
  RotationVector = (1,0,0)
  ScaleType = 0
  ScrubCount = 1
  SeamHidden = false
  SeamVisible = false
  SmoothHidden = false
  SmoothVisible = true
  Source = -> [PolarPattern001Body]
  Type = 0
  X = 148.5
  XDirection = (1,0,0)
  Y = 105
FEATURE [TechDraw::DrawViewDimension] Dimension  label="A"
  AngleOverride = false
  Arbitrary = true
  ArbitraryTolerances = false
  BoxCorners = (2) [(-69.3453,-69.3453,0),(69.3453,69.3453,0)]
  EqualTolerance = true
  ExtensionAngle = 0
  FormatSpec = A
  FormatSpecOverTolerance = %+.2w
  FormatSpecUnderTolerance = %+.2w
  Inverted = false
  LineAngle = 0
  LockPosition = false
  MeasureType = 1
  OverTolerance = 0
  References2D = -> [View]
  Rotation = 0
  ScaleType = 0
  TheoreticalExact = false
  Type = 2
  UnderTolerance = 0
  X = -86.7744
  Y = -4.875
FEATURE [TechDraw::DrawViewDimension] Dimension001  label="B"
  AngleOverride = false
  Arbitrary = true
  ArbitraryTolerances = false
  BoxCorners = (2) [(-69.3453,-69.3453,0),(69.3453,69.3453,0)]
  EqualTolerance = true
  ExtensionAngle = 0
  FormatSpec = B
  FormatSpecOverTolerance = %+.2w
  FormatSpecUnderTolerance = %+.2w
  Inverted = false
  LineAngle = 0
  LockPosition = false
  MeasureType = 1
  OverTolerance = 0
  References2D = -> [View]
  Rotation = 0
  ScaleType = 0
  TheoreticalExact = false
  Type = 1
  UnderTolerance = 0
  X = 0
  Y = 80.7829
FEATURE [TechDraw::DrawViewDimension] Dimension002  label="C"
  AngleOverride = false
  Arbitrary = true
  ArbitraryTolerances = false
  BoxCorners = (2) [(-69.3453,-69.3453,0),(69.3453,69.3453,0)]
  EqualTolerance = true
  ExtensionAngle = 0
  FormatSpec = C
  FormatSpecOverTolerance = %+.2w
  FormatSpecUnderTolerance = %+.2w
  Inverted = false
  LineAngle = 0
  LockPosition = false
  MeasureType = 1
  OverTolerance = 0
  References2D = -> [View]
  Rotation = 0
  ScaleType = 0
  TheoreticalExact = false
  Type = 5
  UnderTolerance = 0
  X = 9.27899
  Y = -22.3726
FEATURE [TechDraw::DrawPage] Page
  KeepUpdated = true
  NextBalloonIndex = 1
  ProjectionType = 0
  Template = -> Template
  Views = -> [View,Dimension,Dimension001,Dimension002]
---- part Stator_CoilWinder_Pins_Quadrilateral.FCStd = doc fcstd_a94792b80ffc ----
FCSTD DOCUMENT  (FreeCAD 1.0R39109 (Git))
Label: Stator_CoilWinder_Pins_Quadrilateral
License: All rights reserved
LicenseURL: http://en.wikipedia.org/wiki/All_rights_reserved
objects: PartDesign::SubShapeBinder×1, Part::Extrusion×1, Part::Mirroring×1, App::Part×1, Spreadsheet::Sheet×1
note: 3 computed .brp shape members not serialized (recipe doc carries the construction recipe); baked Part::Feature solids carry a one-line shape summary decoded from their .brp
EXTERNAL_REF file=Stator_CoilWinder_Cheek.FCStd obj=PolarPattern001Body
EXTERNAL_REF file=../../../Master_of_Puppets.FCStd obj=Alternator

FEATURE [PartDesign::SubShapeBinder] Binder  label="PinHolesSketchBinder"
  BindCopyOnChange = 0
  BindMode = 0
  ClaimChildren = false
  Context = -> Part [Binder.]
  Fuse = false
  MakeFace = true
  OffsetFill = false
  OffsetIntersection = false
  OffsetJoinType = 0
  OffsetOpenResult = false
  PartialLoad = false
  Relative = true
  Support = -> [<external Stator_CoilWinder_Cheek.FCStd>#PolarPattern001Body[Sketch002.]]
  _Version = 2
FEATURE [Part::Extrusion] Extrude
  Base = -> Binder
  Dir = (0,0,1)
  DirMode = 2
  FaceMakerClass = Part::FaceMakerBullseye
  FaceMakerMode = 3
  LengthFwd = 199.4
  LengthRev = 0
  Solid = false
  Symmetric = false
  expr: LengthFwd = Spreadsheet.CoilWinderPinLength
FEATURE [Part::Mirroring] Part__Mirroring  label="Mirror"
  Base = (0,0,0)
  Normal = (1,0,0)
  Source = -> Extrude
FEATURE [App::Part] Part  label="Stator_CoilWinder_Pins"
  Group = -> [Extrude,Binder,Part__Mirroring]
  Origin = -> Origin
FEATURE [Spreadsheet::Sheet] Spreadsheet
  cells = A1='Inputs; A2='CoilWinderPinLength; B2(CoilWinderPinLength)==Master_of_Puppets#Alternator.CoilWinderPinLength
---- part Stator_CoilWinder_Pins_Triangular.FCStd = doc fcstd_adf93230f41c ----
FCSTD DOCUMENT  (FreeCAD 0.20R29177 (Git))
Label: Stator_CoilWinder_Pins_Triangular
License: All rights reserved
LicenseURL: http://en.wikipedia.org/wiki/All_rights_reserved
objects: PartDesign::SubShapeBinder×1, Part::Extrusion×1, Spreadsheet::Sheet×1
note: 2 computed .brp shape members not serialized (recipe doc carries the construction recipe); baked Part::Feature solids carry a one-line shape summary decoded from their .brp
EXTERNAL_REF file=Stator_CoilWinder_Cheek_Triangular.FCStd obj=PolarPattern001Body
EXTERNAL_REF file=../../../Master_of_Puppets.FCStd obj=Alternator

FEATURE [PartDesign::SubShapeBinder] Binder  label="HolesSketchBinder"
  BindCopyOnChange = 0
  BindMode = 0
  ClaimChildren = false
  Fuse = false
  MakeFace = true
  OffsetFill = false
  OffsetIntersection = false
  OffsetJoinType = 0
  OffsetOpenResult = false
  PartialLoad = false
  Relative = true
  Support = -> [<external Stator_CoilWinder_Cheek_Triangular.FCStd>#PolarPattern001Body[Pocket001.Sketch006.]]
  _Version = 2
FEATURE [Part::Extrusion] Extrude  label="Stator_CoilWinder_Pins"
  Base = -> Binder
  Dir = (0,0,1)
  DirMode = 2
  FaceMakerClass = Part::FaceMakerBullseye
  LengthFwd = 202.52
  LengthRev = 0
  Solid = false
  Symmetric = false
  expr: LengthFwd = Spreadsheet.CoilWinderPinLength
FEATURE [Spreadsheet::Sheet] Spreadsheet
  cells = A1=Inputs; A2=CoilWinderPinLength; B2(CoilWinderPinLength)==Master_of_Puppets#Alternator.CoilWinderPinLength
---- part Stator_CoilWinder_Spacer.FCStd = doc fcstd_06fe2c396a98 ----
FCSTD DOCUMENT  (FreeCAD 0.21R33771 (Git))
Label: Stator_CoilWinder_Spacer
License: All rights reserved
LicenseURL: http://en.wikipedia.org/wiki/All_rights_reserved
objects: Sketcher::SketchObject×1, PartDesign::Pad×1, Spreadsheet::Sheet×1, PartDesign::Mirrored×1, PartDesign::Body×1, Part::Refine×1
note: 6 computed .brp shape members not serialized (recipe doc carries the construction recipe); baked Part::Feature solids carry a one-line shape summary decoded from their .brp
EXTERNAL_REF file=../../../Master_of_Puppets.FCStd obj=Alternator
EXTERNAL_REF file=../../../Master_of_Puppets.FCStd obj=Spreadsheet

FEATURE [Sketcher::SketchObject] Sketch
  FullyConstrained = true
  MapMode = 5
  Support = -> [XY_Plane001]
  expr: Constraints[11] = Spreadsheet.OuterHorizontalDistanceFromCenter
  expr: Constraints[17] = Spreadsheet.RectangularVerticalDistanceOfHolesFromCenter * 2
  expr: Constraints[31] = Spreadsheet.CoilWinderPinRadius
  expr: Constraints[43] = Spreadsheet.InnerAngleConstraint
  expr: Constraints[44] = Spreadsheet.InnerHorizontalDistanceFromCenter
  expr: Constraints[45] = Spreadsheet.OuterAngleConstraint
  expr: Constraints[8] = Spreadsheet.CoilWinderCenterRodRadius
  sketch-geometry (19):
    g0: LineSegment StartX=12.5 StartY=20.5 StartZ=0 EndX=0 EndY=20.5 EndZ=0
    g1: LineSegment StartX=0 StartY=20.5 StartZ=0 EndX=0 EndY=5 EndZ=0
    g2: ArcOfCircle CenterX=0 CenterY=0 CenterZ=0 NormalX=0 NormalY=0 NormalZ=1 AngleXU=0 Radius=5 StartAngle=4.71239 EndAngle=7.85398
    g3: LineSegment StartX=-9e-16 StartY=-5 StartZ=0 EndX=0 EndY=-20.5 EndZ=0
    g4: LineSegment StartX=0 StartY=20.5 StartZ=0 EndX=0 EndY=5 EndZ=0
    g5: LineSegment StartX=12.5 StartY=20.5 StartZ=0 EndX=12.5 EndY=-20.5 EndZ=0
    g6: LineSegment StartX=12.5 StartY=-20.5 StartZ=0 EndX=0 EndY=-20.5 EndZ=0
    g7: GeomPoint X=10.7322 Y=18.7322 Z=0
    g8: LineSegment StartX=10.7322 StartY=18.7322 StartZ=0 EndX=12.5 EndY=16.9645 EndZ=0
    g9: LineSegment StartX=12.5 StartY=16.9645 StartZ=0 EndX=12.5 EndY=-16.9645 EndZ=0
    g10: LineSegment StartX=12.5 StartY=-16.9645 StartZ=0 EndX=10.7322 EndY=-18.7322 EndZ=0
    g11: LineSegment StartX=10.7322 StartY=-18.7322 StartZ=0 EndX=8.96447 EndY=-20.5 EndZ=0
    g12: LineSegment StartX=8.96447 StartY=-20.5 StartZ=0 EndX=0 EndY=-20.5 EndZ=0
    g13: LineSegment StartX=10.7322 StartY=18.7322 StartZ=0 EndX=8.96447 EndY=20.5 EndZ=0
    g14: LineSegment StartX=8.96447 StartY=20.5 StartZ=0 EndX=0 EndY=20.5 EndZ=0
    g15: Circle CenterX=12.5 CenterY=20.5 CenterZ=0 NormalX=0 NormalY=0 NormalZ=1 AngleXU=0 Radius=2.5
    g16: Circle CenterX=12.5 CenterY=-20.5 CenterZ=0 NormalX=0 NormalY=0 NormalZ=1 AngleXU=0 Radius=2.5
    g17: LineSegment StartX=10.7322 StartY=18.7322 StartZ=0 EndX=12.5 EndY=20.5 EndZ=0
    g18: LineSegment StartX=12.5 StartY=-20.5 StartZ=0 EndX=10.7322 EndY=-18.7322 EndZ=0
  constraints (46):
    c: Coincident(g1,g0)
    c: Vertical(g1)
    c: PointOnObject(g0,g-2)
    c: Horizontal(g0)
    c: Coincident(g2,g-1)
    c: Coincident(g2,g1)
    c: PointOnObject(g2,g-2)
    c: Coincident(g2,g3)
    c: Radius(g2) = 5
    c: Coincident(g4,g0)
    c: Coincident(g4,g1)
    c: Distance(g0) = 12.5
    c: Coincident(g5,g0)
    c: Coincident(g6,g5)
    c: Horizontal(g6)
    c: Coincident(g3,g6)
    c: Symmetric(g3,g0,g-1)
    c: DistanceY(g5,g0) = 41
    c: Coincident(g8,g7)
    c: PointOnObject(g8,g5)
    c: Coincident(g9,g8)
    c: PointOnObject(g9,g5)
    c: Coincident(g10,g9)
    c: PointOnObject(g11,g6)
    c: Coincident(g12,g11)
    c: Coincident(g12,g3)
    c: Coincident(g13,g8)
    c: PointOnObject(g13,g0)
    c: Coincident(g14,g13)
    c: Coincident(g14,g4)
    c: Coincident(g15,g0)
    c: Radius(g15) = 2.5
    c: Coincident(g16,g5)
    c: Equal(g16,g15)
    c: Parallel(g8,g13)
    c: Tangent(g8,g15) = -1.5708
    c: Coincident(g17,g8)
    c: Coincident(g17,g0)
    c: Coincident(g10,g11)
    c: Parallel(g10,g11)
    c: Tangent(g10,g16) = -1.5708
    c: Coincident(g18,g5)
    c: Coincident(g18,g10)
    c: Angle(g18,g6) = 0.785398
    c: DistanceX(g-1,g5) = 12.5
    c: Angle(g0,g17) = 0.785398
FEATURE [PartDesign::Pad] Pad
  AllowMultiFace = false
  Direction = (0,0,1)
  Length = 13
  Length2 = 100
  Profile = -> Sketch
  Type = 0
  expr: Length = Spreadsheet.StatorThickness
FEATURE [Spreadsheet::Sheet] Spreadsheet
  cells = A1='Inputs; A2='Spreadsheet; A3='MagnetLength; B3(MagnetLength)==Master_of_Puppets#Spreadsheet.MagnetLength; A4='StatorThickness; B4(StatorThickness)==Master_of_Puppets#Spreadsheet.StatorThickness; A5='CoilHoleWidthAtOuterRadius; B5(CoilHoleWidthAtOuterRadius)==Master_of_Puppets#Spreadsheet.CoilHoleWidthAtOuterRadius; A6='CoilHoleWidthAtInnerRadius; B6(CoilHoleWidthAtInnerRadius)==Master_of_Puppets#Spreadsheet.CoilHoleWidthAtInnerRadius; A7='CoilType; B7(CoilType)==Master_of_Puppets#Spreadsheet.CoilType; A8='Alternator; A9='CoilWinderCenterRodRadius; B9(CoilWinderCenterRodRadius)==Master_of_Puppets#Alternator.CoilWinderCenterRodRadius; A10='CoilWinderPinRadius; B10(CoilWinderPinRadius)==Master_of_Puppets#Alternator.CoilWinderPinRadius; A11='RectangularVerticalDistanceOfHolesFromCenter; B11(RectangularVerticalDistanceOfHolesFromCenter)==Master_of_Puppets#Alternator.RectangularVerticalDistanceOfHolesFromCenter; A12='OuterHorizontalDistanceBetweenCenterOfSmallHoles; B12(OuterHorizontalDistanceBetweenCenterOfSmallHoles)==Master_of_Puppets#Alternator.OuterHorizontalDistanceBetweenCenterOfSmallHoles; A13='InnerHorizontalDistanceBetweenCenterOfSmallHoles; B13(InnerHorizontalDistanceBetweenCenterOfSmallHoles)==Master_of_Puppets#Alternator.InnerHorizontalDistanceBetweenCenterOfSmallHoles; A14='Calculated; A15='OuterHorizontalDistanceFromCenter; B15(OuterHorizontalDistanceFromCenter)==OuterHorizontalDistanceBetweenCenterOfSmallHoles / 2; A16='InnerHorizontalDistanceFromCenter; B16(InnerHorizontalDistanceFromCenter)==InnerHorizontalDistanceBetweenCenterOfSmallHoles / 2; A17='OuterPoint; B17(OuterPoint)==create(<<vector>>; OuterHorizontalDistanceFromCenter; RectangularVerticalDistanceOfHolesFromCenter; 0); A18='InnerPoint; B18(InnerPoint)==create(<<vector>>; InnerHorizontalDistanceFromCenter; -RectangularVerticalDistanceOfHolesFromCenter; 0); A19='InnerToOuterVector; B19(InnerToOuterVector)==OuterPoint - InnerPoint; A20='AngleBetweenXAxis; B20(AngleBetweenXAxis)==acos(.InnerToOuterVector.x / .InnerToOuterVector.Length); A21='OuterAngleConstraint; B21(OuterAngleConstraint)==AngleBetweenXAxis / 2; A22='InnerAngleConstraint; B22(InnerAngleConstraint)==(180 deg - AngleBetweenXAxis) / 2
FEATURE [PartDesign::Mirrored] Mirrored
  BaseFeature = -> Pad
  MirrorPlane = -> Sketch [V_Axis]
  Originals = -> [Pad]
FEATURE [PartDesign::Body] PadBody  label="Body"
  Group = -> [Sketch,Pad,Mirrored]
  Origin = -> Origin001
  Tip = -> Mirrored
FEATURE [Part::Refine] PadBody001  label="Stator_CoilWinder_Spacer"
  Openafpm_Flat = true
  Source = -> PadBody
---- part Stator_CoilWinder_Spacer_Triangular.FCStd = doc fcstd_b6fa446f0f1e ----
FCSTD DOCUMENT  (FreeCAD 0.21R33771 (Git))
Label: Stator_CoilWinder_Spacer_Triangular
License: All rights reserved
LicenseURL: http://en.wikipedia.org/wiki/All_rights_reserved
objects: Sketcher::SketchObject×1, PartDesign::Pad×1, Spreadsheet::Sheet×1, PartDesign::Mirrored×1, PartDesign::Body×1, Part::Refine×1
note: 6 computed .brp shape members not serialized (recipe doc carries the construction recipe); baked Part::Feature solids carry a one-line shape summary decoded from their .brp
EXTERNAL_REF file=../../../Master_of_Puppets.FCStd obj=Alternator
EXTERNAL_REF file=../../../Master_of_Puppets.FCStd obj=Spreadsheet

FEATURE [Sketcher::SketchObject] Sketch
  FullyConstrained = true
  MapMode = 5
  Support = -> [XY_Plane001]
  expr: Constraints[17] = Spreadsheet.CoilWinderCenterRodRadius
  expr: Constraints[23] = Spreadsheet.TriangularCoilWinderCircumradius
  expr: Constraints[24] = Spreadsheet.HorizontalDistanceBetweenPins
  expr: Constraints[35] = Spreadsheet.DistanceBetweenTriangularCoilAndTapeNotch
  expr: Constraints[38] = Spreadsheet.DistanceBetweenTriangularCoilAndTapeNotch
  expr: Constraints[46] = Spreadsheet.CoilWinderPinRadius * 2
  expr: Constraints[54] = Spreadsheet.CoilWinderPinRadius * 2
  expr: Constraints[7] = Spreadsheet.BottomHoleRadius
  expr: Constraints[8] = Spreadsheet.CoilWinderPinRadius
  sketch-geometry (21):
    g0: LineSegment StartX=0 StartY=-26 StartZ=0 EndX=20 EndY=15 EndZ=0
    g1: LineSegment StartX=20 StartY=15 StartZ=0 EndX=-20 EndY=15 EndZ=0
    g2: LineSegment StartX=-20 StartY=15 StartZ=0 EndX=0 EndY=-26 EndZ=0
    g3: Circle CenterX=0 CenterY=0 CenterZ=0 NormalX=0 NormalY=0 NormalZ=1 AngleXU=0 Radius=30
    g4: Circle CenterX=0 CenterY=-26 CenterZ=0 NormalX=0 NormalY=0 NormalZ=1 AngleXU=0 Radius=4
    g5: Circle CenterX=-20 CenterY=15 CenterZ=0 NormalX=0 NormalY=0 NormalZ=1 AngleXU=0 Radius=5
    g6: Circle CenterX=20 CenterY=15 CenterZ=0 NormalX=0 NormalY=0 NormalZ=1 AngleXU=0 Radius=5
    g7: LineSegment StartX=-13.75 StartY=15 StartZ=0 EndX=13.75 EndY=15 EndZ=0
    g8: LineSegment StartX=1.95122 StartY=-22 StartZ=0 EndX=-1.95122 EndY=-22 EndZ=0
    g9: Circle CenterX=0 CenterY=0 CenterZ=0 NormalX=0 NormalY=0 NormalZ=1 AngleXU=0 Radius=5
    g10: LineSegment StartX=13.75 StartY=15 StartZ=0 EndX=20 EndY=15 EndZ=0
    g11: LineSegment StartX=19.4553 StartY=7.39293 StartZ=0 EndX=4.31084 EndY=-22 EndZ=0
    g12: LineSegment StartX=4.31084 StartY=-22 StartZ=0 EndX=1.95122 EndY=-22 EndZ=0
    g13: LineSegment StartX=-19.4553 StartY=7.39292 StartZ=0 EndX=-4.31084 EndY=-22 EndZ=0
    g14: LineSegment StartX=-4.31084 StartY=-22 StartZ=0 EndX=-1.95122 EndY=-22 EndZ=0
    g15: LineSegment StartX=-24.4447 StartY=12.7099 StartZ=0 EndX=-3.55577 EndY=-27.8321 EndZ=0
    g16: LineSegment StartX=3.55577 StartY=-27.8321 StartZ=0 EndX=24.4447 EndY=12.7099 EndZ=0
    g17: LineSegment StartX=-19.4553 StartY=7.39292 StartZ=0 EndX=-13.75 EndY=15 EndZ=0
    g18: LineSegment StartX=-20 StartY=15 StartZ=0 EndX=-24 EndY=18 EndZ=0
    g19: LineSegment StartX=13.75 StartY=15 StartZ=0 EndX=19.4553 EndY=7.39293 EndZ=0
    g20: LineSegment StartX=20 StartY=15 StartZ=0 EndX=24 EndY=18 EndZ=0
  constraints (55):
    c: Coincident(g0,g1)
    c: Coincident(g1,g2)
    c: Coincident(g2,g0)
    c: Equal(g0,g2)
    c: Coincident(g3,g-1)
    c: Tangent(g4,g3)
    c: PointOnObject(g4,g-2)
    c: Radius(g4) = 4
    c: Radius(g5) = 5
    c: Equal(g6,g5)
    c: PointOnObject(g7,g1)
    c: PointOnObject(g7,g1)
    c: PointOnObject(g8,g0)
    c: PointOnObject(g8,g2)
    c: Tangent(g8,g4)
    c: Horizontal(g8)
    c: Coincident(g9,g-1)
    c: Radius(g9) = 5
    c: Coincident(g10,g7)
    c: Coincident(g10,g0)
    c: Coincident(g0,g6)
    c: Coincident(g5,g1)
    c: Coincident(g0,g4)
    c: Radius(g3) = 30
    c: DistanceX(g1,g0) = 40
    c: Tangent(g3,g6)
    c: Horizontal(g11,g8)
    c: Coincident(g12,g11)
    c: Coincident(g12,g8)
    c: Horizontal(g13,g8)
    c: Coincident(g14,g13)
    c: Coincident(g14,g8)
    c: Tangent(g15,g5) = -1.5708
    c: Tangent(g15,g4) = -1.5708
    c: Parallel(g13,g15)
    c: Distance(g13,g15) = 2
    c: Tangent(g16,g6) = -1.5708
    c: Tangent(g16,g4) = -1.5708
    c: Distance(g11,g16) = 2
    c: Parallel(g16,g11)
    c: Coincident(g17,g13)
    c: Coincident(g17,g7)
    c: Horizontal(g1)
    c: Coincident(g18,g1)
    c: PointOnObject(g18,g3)
    c: PointOnObject(g18,g5)
    c: Distance(g18,g17) = 10
    c: Tangent(g17,g5)
    c: Coincident(g19,g7)
    c: Coincident(g19,g11)
    c: Tangent(g19,g6)
    c: Coincident(g20,g0)
    c: PointOnObject(g20,g6)
    c: PointOnObject(g20,g3)
    c: Distance(g20,g19) = 10
FEATURE [PartDesign::Pad] Pad
  AllowMultiFace = false
  Direction = (0,0,1)
  Length = 13
  Length2 = 100
  Profile = -> Sketch
  Type = 0
  expr: Length = Spreadsheet.StatorThickness
FEATURE [Spreadsheet::Sheet] Spreadsheet
  cells = A1='Inputs; A2='Spreadsheet; A3='MagnetWidth; B3(MagnetWidth)==Master_of_Puppets#Spreadsheet.MagnetWidth; A4='StatorThickness; B4(StatorThickness)==Master_of_Puppets#Spreadsheet.StatorThickness; A5='CoilHoleWidthAtInnerRadius; B5(CoilHoleWidthAtInnerRadius)==Master_of_Puppets#Spreadsheet.CoilHoleWidthAtInnerRadius; A6='CoilType; B6(CoilType)==Master_of_Puppets#Spreadsheet.CoilType; A7='HorizontalDistanceBetweenPins; B7(HorizontalDistanceBetweenPins)==Master_of_Puppets#Alternator.TriangularHorizontalDistanceBetweenPins; A8='Alternator; A9='CoilWinderCenterRodRadius; B9(CoilWinderCenterRodRadius)==Master_of_Puppets#Alternator.CoilWinderCenterRodRadius; A10='CoilWinderPinRadius; B10(CoilWinderPinRadius)==Master_of_Puppets#Alternator.CoilWinderPinRadius; A11='BottomHoleRadius; B11(BottomHoleRadius)==Master_of_Puppets#Alternator.CoilWinderDiskBottomHoleRadius; A12='TriangularCoilWinderCircumradius; B12(TriangularCoilWinderCircumradius)==Master_of_Puppets#Alternator.TriangularCoilWinderCircumradius; A13='DistanceBetweenTriangularCoilAndTapeNotch; B13(DistanceBetweenTriangularCoilAndTapeNotch)==Master_of_Puppets#Alternator.DistanceBetweenTriangularCoilAndTapeNotch
FEATURE [PartDesign::Mirrored] Mirrored
  BaseFeature = -> Pad
  MirrorPlane = -> Sketch [V_Axis]
  Originals = -> [Pad]
FEATURE [PartDesign::Body] PadBody  label="Body"
  Group = -> [Sketch,Pad,Mirrored]
  Origin = -> Origin001
  Tip = -> Mirrored
FEATURE [Part::Refine] PadBody001  label="Stator_CoilWinder_Spacer"
  Openafpm_Flat = true
  Source = -> PadBody
